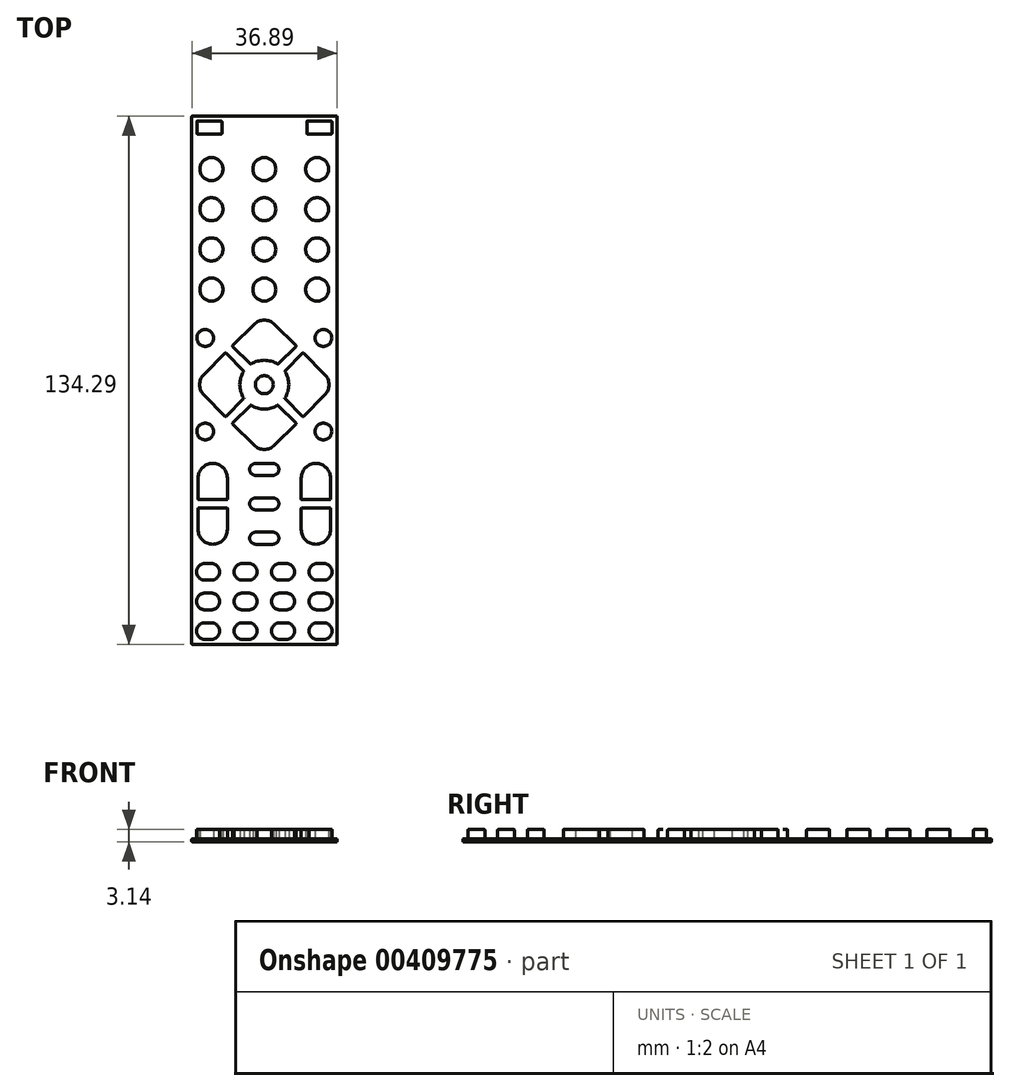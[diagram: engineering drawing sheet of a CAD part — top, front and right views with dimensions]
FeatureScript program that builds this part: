
annotation { "Feature Type Name" : "Feature", "Feature Type Description" : "" }
export const myFeature = defineFeature(function(context is Context, id is Id, definition is map)
    precondition{}
    {
        {
            var Q0;
            Q0=qCreatedBy(makeId("Top.planeOp"),FACE);
            var sketch = newSketch(context, id + "F0", { "sketchPlane" : qUnion([Q0])});
            skLineSegment(sketch, "E0", {"start": v(0, 71.3) * mm, "end": v(0, -90.63) * mm, "construction": true});
            skLineSegment(sketch, "E1.bottom", {"start": v(-17.4, 63.46) * mm, "end": v(-10.54, 63.46) * mm});
            skLineSegment(sketch, "E1.top", {"start": v(-17.4, 67.27) * mm, "end": v(-10.54, 67.27) * mm});
            skLineSegment(sketch, "E1.left", {"start": v(-17.4, 63.46) * mm, "end": v(-17.4, 67.27) * mm});
            skLineSegment(sketch, "E1.right", {"start": v(-10.54, 63.46) * mm, "end": v(-10.54, 67.27) * mm});
            skLineSegment(sketch, "E2.bottom", {"start": v(10.54, 63.46) * mm, "end": v(17.4, 63.46) * mm});
            skLineSegment(sketch, "E2.top", {"start": v(10.54, 67.27) * mm, "end": v(17.4, 67.27) * mm});
            skLineSegment(sketch, "E2.left", {"start": v(10.54, 63.46) * mm, "end": v(10.54, 67.27) * mm});
            skLineSegment(sketch, "E2.right", {"start": v(17.4, 63.46) * mm, "end": v(17.4, 67.27) * mm});
            skCircle(sketch, "E3", {"center": v(-13.44, 54.79) * mm, "radius": 3.18 * mm});
            skCircle(sketch, "E4.0.1.0", {"center": v(-13.44, 44.59) * mm, "radius": 3.18 * mm});
            skLineSegment(sketch, "E4.0.1.1", {"start": v(0, 61.1) * mm, "end": v(0, -100.83) * mm, "construction": true});
            skCircle(sketch, "E4.0.2.0", {"center": v(-13.44, 34.39) * mm, "radius": 3.18 * mm});
            skLineSegment(sketch, "E4.0.2.1", {"start": v(0, 50.9) * mm, "end": v(0, -111.03) * mm, "construction": true});
            skCircle(sketch, "E4.0.3.0", {"center": v(-13.44, 24.18) * mm, "radius": 3.18 * mm});
            skLineSegment(sketch, "E4.0.3.1", {"start": v(0, 40.7) * mm, "end": v(0, -121.23) * mm, "construction": true});
            skCircle(sketch, "E4.1.0.0", {"center": v(0, 54.79) * mm, "radius": 3.18 * mm});
            skLineSegment(sketch, "E4.1.0.1", {"start": v(13.44, 71.3) * mm, "end": v(13.44, -90.63) * mm, "construction": true});
            skCircle(sketch, "E4.1.1.0", {"center": v(0, 44.59) * mm, "radius": 3.18 * mm});
            skLineSegment(sketch, "E4.1.1.1", {"start": v(13.44, 61.1) * mm, "end": v(13.44, -100.83) * mm, "construction": true});
            skCircle(sketch, "E4.1.2.0", {"center": v(0, 34.39) * mm, "radius": 3.18 * mm});
            skLineSegment(sketch, "E4.1.2.1", {"start": v(13.44, 50.9) * mm, "end": v(13.44, -111.03) * mm, "construction": true});
            skCircle(sketch, "E4.1.3.0", {"center": v(0, 24.18) * mm, "radius": 3.18 * mm});
            skLineSegment(sketch, "E4.1.3.1", {"start": v(13.44, 40.7) * mm, "end": v(13.44, -121.23) * mm, "construction": true});
            skCircle(sketch, "E4.2.0.0", {"center": v(13.44, 54.79) * mm, "radius": 3.18 * mm});
            skLineSegment(sketch, "E4.2.0.1", {"start": v(26.87, 71.3) * mm, "end": v(26.87, -90.63) * mm, "construction": true});
            skCircle(sketch, "E4.2.1.0", {"center": v(13.44, 44.59) * mm, "radius": 3.18 * mm});
            skLineSegment(sketch, "E4.2.1.1", {"start": v(26.87, 61.1) * mm, "end": v(26.87, -100.83) * mm, "construction": true});
            skCircle(sketch, "E4.2.2.0", {"center": v(13.44, 34.39) * mm, "radius": 3.18 * mm});
            skLineSegment(sketch, "E4.2.2.1", {"start": v(26.87, 50.9) * mm, "end": v(26.87, -111.03) * mm, "construction": true});
            skCircle(sketch, "E4.2.3.0", {"center": v(13.44, 24.18) * mm, "radius": 3.18 * mm});
            skLineSegment(sketch, "E4.2.3.1", {"start": v(26.87, 40.7) * mm, "end": v(26.87, -121.23) * mm, "construction": true});
            skLineSegment(sketch, "E4.direction1", {"start": v(-13.44, 54.79) * mm, "end": v(0, 54.79) * mm, "construction": true});
            skLineSegment(sketch, "E4.direction2", {"start": v(-13.44, 54.79) * mm, "end": v(-13.44, 44.59) * mm, "construction": true});
            skCircle(sketch, "E5", {"center": v(0, 0) * mm, "radius": 2.54 * mm});
            skCircle(sketch, "E6", {"center": v(-15.02, 11.88) * mm, "radius": 2.38 * mm});
            skLineSegment(sketch, "E7", {"start": v(-22.23, 0) * mm, "end": v(22.23, 0) * mm, "construction": true});
            skCircle(sketch, "E8.MirrorC", {"center": v(15.02, 11.88) * mm, "radius": 2.38 * mm});
            skCircle(sketch, "E9.MirrorC", {"center": v(15.02, -11.88) * mm, "radius": 2.38 * mm});
            skCircle(sketch, "E10.MirrorC", {"center": v(-15.02, -11.88) * mm, "radius": 2.38 * mm});
            skArc(sketch, "E11", {"start": v(-15.54, 2.78) * mm, "mid": v(-16.7, 0) * mm, "end": v(-15.54, -2.78) * mm});
            skLineSegment(sketch, "E12", {"start": v(-15.54, 2.78) * mm, "end": v(-9.83, 8.49) * mm});
            skLineSegment(sketch, "E13", {"start": v(-9.83, 8.49) * mm, "end": v(-4.84, 3.5) * mm});
            skLineSegment(sketch, "E14", {"start": v(-15.54, -2.78) * mm, "end": v(-9.83, -8.49) * mm});
            skLineSegment(sketch, "E15", {"start": v(-9.83, -8.49) * mm, "end": v(-4.84, -3.5) * mm});
            skArc(sketch, "E16", {"start": v(-4.84, 3.5) * mm, "mid": v(-5.97, 0) * mm, "end": v(-4.84, -3.5) * mm});
            skLineSegment(sketch, "E17.MirrorCS", {"start": v(0, -61.1) * mm, "end": v(0, 100.83) * mm, "construction": true});
            skLineSegment(sketch, "E18.1.0", {"start": v(-2.78, -15.54) * mm, "end": v(-8.49, -9.83) * mm});
            skLineSegment(sketch, "E18.1.1", {"start": v(-8.49, -9.83) * mm, "end": v(-3.5, -4.84) * mm});
            skArc(sketch, "E18.1.2", {"start": v(-3.5, -4.84) * mm, "mid": v(0, -5.97) * mm, "end": v(3.5, -4.84) * mm});
            skLineSegment(sketch, "E18.1.3", {"start": v(8.49, -9.83) * mm, "end": v(3.5, -4.84) * mm});
            skLineSegment(sketch, "E18.1.4", {"start": v(2.78, -15.54) * mm, "end": v(8.49, -9.83) * mm});
            skArc(sketch, "E18.1.5", {"start": v(-2.78, -15.54) * mm, "mid": v(0, -16.7) * mm, "end": v(2.78, -15.54) * mm});
            skLineSegment(sketch, "E18.2.0", {"start": v(15.54, -2.78) * mm, "end": v(9.83, -8.49) * mm});
            skLineSegment(sketch, "E18.2.1", {"start": v(9.83, -8.49) * mm, "end": v(4.84, -3.5) * mm});
            skArc(sketch, "E18.2.2", {"start": v(4.84, -3.5) * mm, "mid": v(5.97, 0) * mm, "end": v(4.84, 3.5) * mm});
            skLineSegment(sketch, "E18.2.3", {"start": v(9.83, 8.49) * mm, "end": v(4.84, 3.5) * mm});
            skLineSegment(sketch, "E18.2.4", {"start": v(15.54, 2.78) * mm, "end": v(9.83, 8.49) * mm});
            skArc(sketch, "E18.2.5", {"start": v(15.54, -2.78) * mm, "mid": v(16.7, 0) * mm, "end": v(15.54, 2.78) * mm});
            skLineSegment(sketch, "E18.3.0", {"start": v(2.78, 15.54) * mm, "end": v(8.49, 9.83) * mm});
            skLineSegment(sketch, "E18.3.1", {"start": v(8.49, 9.83) * mm, "end": v(3.5, 4.84) * mm});
            skArc(sketch, "E18.3.2", {"start": v(3.5, 4.84) * mm, "mid": v(0, 5.97) * mm, "end": v(-3.5, 4.84) * mm});
            skLineSegment(sketch, "E18.3.3", {"start": v(-8.49, 9.83) * mm, "end": v(-3.5, 4.84) * mm});
            skLineSegment(sketch, "E18.3.4", {"start": v(-2.78, 15.54) * mm, "end": v(-8.49, 9.83) * mm});
            skArc(sketch, "E18.3.5", {"start": v(2.78, 15.54) * mm, "mid": v(0, 16.7) * mm, "end": v(-2.78, 15.54) * mm});
            skPoint(sketch, "E19.visualSharp", {"position": v(9.83, 8.49) * mm});
            skPoint(sketch, "E20.visualSharp", {"position": v(4.84, 3.5) * mm});
            skPoint(sketch, "E21.visualSharp", {"position": v(4.84, -3.5) * mm});
            skPoint(sketch, "E22.visualSharp", {"position": v(9.83, -8.49) * mm});
            skPoint(sketch, "E23.visualSharp", {"position": v(3.5, -4.84) * mm});
            skPoint(sketch, "E24.visualSharp", {"position": v(8.49, -9.83) * mm});
            skPoint(sketch, "E25.visualSharp", {"position": v(-8.49, -9.83) * mm});
            skPoint(sketch, "E26.visualSharp", {"position": v(-3.5, -4.84) * mm});
            skPoint(sketch, "E27.visualSharp", {"position": v(-9.83, -8.49) * mm});
            skPoint(sketch, "E28.visualSharp", {"position": v(-4.84, -3.5) * mm});
            skPoint(sketch, "E29.visualSharp", {"position": v(-4.84, 3.5) * mm});
            skPoint(sketch, "E30.visualSharp", {"position": v(-9.83, 8.49) * mm});
            skPoint(sketch, "E31.visualSharp", {"position": v(8.49, 9.83) * mm});
            skPoint(sketch, "E32.visualSharp", {"position": v(3.5, 4.84) * mm});
            skPoint(sketch, "E33.visualSharp", {"position": v(-3.5, 4.84) * mm});
            skPoint(sketch, "E34.visualSharp", {"position": v(-8.49, 9.83) * mm});
            skLineSegment(sketch, "E35", {"start": v(-2.18, -21.53) * mm, "end": v(2.18, -21.53) * mm, "construction": true});
            skArc(sketch, "E36.0.startCap", {"start": v(-2.18, -23.31) * mm, "mid": v(-3.97, -21.53) * mm, "end": v(-2.18, -19.74) * mm});
            skArc(sketch, "E36.0.endCap", {"start": v(2.18, -19.74) * mm, "mid": v(3.97, -21.53) * mm, "end": v(2.18, -23.31) * mm});
            skLineSegment(sketch, "E36.0.left", {"start": v(-2.18, -19.74) * mm, "end": v(2.18, -19.74) * mm});
            skLineSegment(sketch, "E36.0.right", {"start": v(-2.18, -23.31) * mm, "end": v(2.18, -23.31) * mm});
            skLineSegment(sketch, "E37.0.1.0", {"start": v(-2.18, -28.47) * mm, "end": v(2.18, -28.47) * mm});
            skArc(sketch, "E37.0.1.1", {"start": v(2.18, -28.47) * mm, "mid": v(3.97, -30.26) * mm, "end": v(2.18, -32.05) * mm});
            skLineSegment(sketch, "E37.0.1.2", {"start": v(-2.18, -32.05) * mm, "end": v(2.18, -32.05) * mm});
            skArc(sketch, "E37.0.1.3", {"start": v(-2.18, -32.05) * mm, "mid": v(-3.97, -30.26) * mm, "end": v(-2.18, -28.47) * mm});
            skLineSegment(sketch, "E37.0.2.0", {"start": v(-2.18, -37.2) * mm, "end": v(2.18, -37.2) * mm});
            skArc(sketch, "E37.0.2.1", {"start": v(2.18, -37.2) * mm, "mid": v(3.97, -39) * mm, "end": v(2.18, -40.78) * mm});
            skLineSegment(sketch, "E37.0.2.2", {"start": v(-2.18, -40.78) * mm, "end": v(2.18, -40.78) * mm});
            skArc(sketch, "E37.0.2.3", {"start": v(-2.18, -40.78) * mm, "mid": v(-3.97, -39) * mm, "end": v(-2.18, -37.2) * mm});
            skLineSegment(sketch, "E37.direction1", {"start": v(-2.18, -19.74) * mm, "end": v(23.22, -19.74) * mm, "construction": true});
            skLineSegment(sketch, "E37.direction2", {"start": v(-2.18, -19.74) * mm, "end": v(-2.18, -28.47) * mm, "construction": true});
            skLineSegment(sketch, "E38", {"start": v(-2.18, -30.26) * mm, "end": v(2.18, -30.26) * mm, "construction": true});
            skLineSegment(sketch, "E39.bottom", {"start": v(-17.07, -29.47) * mm, "end": v(-9.13, -29.47) * mm});
            skLineSegment(sketch, "E39.left", {"start": v(-17.07, -29.47) * mm, "end": v(-17.07, -23.7) * mm});
            skLineSegment(sketch, "E39.right", {"start": v(-9.13, -29.47) * mm, "end": v(-9.13, -23.7) * mm});
            skArc(sketch, "E40", {"start": v(-9.13, -23.7) * mm, "mid": v(-13.1, -19.74) * mm, "end": v(-17.07, -23.7) * mm});
            skLineSegment(sketch, "E41.MirrorCS", {"start": v(9.13, -29.47) * mm, "end": v(9.13, -23.7) * mm});
            skLineSegment(sketch, "E42.MirrorCS", {"start": v(17.07, -29.47) * mm, "end": v(9.13, -29.47) * mm});
            skLineSegment(sketch, "E43.MirrorCS", {"start": v(17.07, -29.47) * mm, "end": v(17.07, -23.7) * mm});
            skArc(sketch, "E44.MirrorCS", {"start": v(9.13, -23.7) * mm, "mid": v(13.1, -19.74) * mm, "end": v(17.07, -23.7) * mm});
            skLineSegment(sketch, "E45.MirrorCS", {"start": v(17.07, -31.05) * mm, "end": v(9.13, -31.05) * mm});
            skLineSegment(sketch, "E46.MirrorCS", {"start": v(9.13, -31.05) * mm, "end": v(9.13, -36.81) * mm});
            skArc(sketch, "E47.MirrorCS", {"start": v(9.13, -36.81) * mm, "mid": v(13.1, -40.78) * mm, "end": v(17.07, -36.81) * mm});
            skLineSegment(sketch, "E48.MirrorCS", {"start": v(17.07, -31.05) * mm, "end": v(17.07, -36.81) * mm});
            skLineSegment(sketch, "E49.MirrorCS", {"start": v(-17.07, -31.05) * mm, "end": v(-9.13, -31.05) * mm});
            skLineSegment(sketch, "E50.MirrorCS", {"start": v(-9.13, -31.05) * mm, "end": v(-9.13, -36.81) * mm});
            skLineSegment(sketch, "E51.MirrorCS", {"start": v(-17.07, -31.05) * mm, "end": v(-17.07, -36.81) * mm});
            skArc(sketch, "E52.MirrorCS", {"start": v(-9.13, -36.81) * mm, "mid": v(-13.1, -40.78) * mm, "end": v(-17.07, -36.81) * mm});
            skLineSegment(sketch, "E53", {"start": v(-15.08, -47.53) * mm, "end": v(-13.5, -47.53) * mm, "construction": true});
            skArc(sketch, "E54.0.startCap", {"start": v(-15.08, -49.9) * mm, "mid": v(-17.46, -47.53) * mm, "end": v(-15.08, -45.15) * mm});
            skArc(sketch, "E54.0.endCap", {"start": v(-13.5, -45.15) * mm, "mid": v(-11.11, -47.53) * mm, "end": v(-13.5, -49.9) * mm});
            skLineSegment(sketch, "E54.0.left", {"start": v(-15.08, -45.15) * mm, "end": v(-13.5, -45.15) * mm});
            skLineSegment(sketch, "E54.0.right", {"start": v(-15.08, -49.9) * mm, "end": v(-13.5, -49.9) * mm});
            skArc(sketch, "E55.0.1.0", {"start": v(-13.5, -52.69) * mm, "mid": v(-11.11, -55.07) * mm, "end": v(-13.5, -57.45) * mm});
            skLineSegment(sketch, "E55.0.1.1", {"start": v(-15.08, -52.69) * mm, "end": v(-13.5, -52.69) * mm});
            skArc(sketch, "E55.0.1.2", {"start": v(-15.08, -57.45) * mm, "mid": v(-17.46, -55.07) * mm, "end": v(-15.08, -52.69) * mm});
            skLineSegment(sketch, "E55.0.1.3", {"start": v(-15.08, -57.45) * mm, "end": v(-13.5, -57.45) * mm});
            skArc(sketch, "E55.0.2.0", {"start": v(-13.5, -60.23) * mm, "mid": v(-11.11, -62.6) * mm, "end": v(-13.5, -64.99) * mm});
            skLineSegment(sketch, "E55.0.2.1", {"start": v(-15.08, -60.23) * mm, "end": v(-13.5, -60.23) * mm});
            skArc(sketch, "E55.0.2.2", {"start": v(-15.08, -64.99) * mm, "mid": v(-17.46, -62.6) * mm, "end": v(-15.08, -60.23) * mm});
            skLineSegment(sketch, "E55.0.2.3", {"start": v(-15.08, -64.99) * mm, "end": v(-13.5, -64.99) * mm});
            skArc(sketch, "E55.1.0.0", {"start": v(-3.97, -45.15) * mm, "mid": v(-1.59, -47.53) * mm, "end": v(-3.97, -49.9) * mm});
            skLineSegment(sketch, "E55.1.0.1", {"start": v(-5.56, -45.15) * mm, "end": v(-3.97, -45.15) * mm});
            skArc(sketch, "E55.1.0.2", {"start": v(-5.56, -49.9) * mm, "mid": v(-7.94, -47.53) * mm, "end": v(-5.56, -45.15) * mm});
            skLineSegment(sketch, "E55.1.0.3", {"start": v(-5.56, -49.9) * mm, "end": v(-3.97, -49.9) * mm});
            skArc(sketch, "E55.1.1.0", {"start": v(-3.97, -52.69) * mm, "mid": v(-1.59, -55.07) * mm, "end": v(-3.97, -57.45) * mm});
            skLineSegment(sketch, "E55.1.1.1", {"start": v(-5.56, -52.69) * mm, "end": v(-3.97, -52.69) * mm});
            skArc(sketch, "E55.1.1.2", {"start": v(-5.56, -57.45) * mm, "mid": v(-7.94, -55.07) * mm, "end": v(-5.56, -52.69) * mm});
            skLineSegment(sketch, "E55.1.1.3", {"start": v(-5.56, -57.45) * mm, "end": v(-3.97, -57.45) * mm});
            skArc(sketch, "E55.1.2.0", {"start": v(-3.97, -60.23) * mm, "mid": v(-1.59, -62.6) * mm, "end": v(-3.97, -64.99) * mm});
            skLineSegment(sketch, "E55.1.2.1", {"start": v(-5.56, -60.23) * mm, "end": v(-3.97, -60.23) * mm});
            skArc(sketch, "E55.1.2.2", {"start": v(-5.56, -64.99) * mm, "mid": v(-7.94, -62.6) * mm, "end": v(-5.56, -60.23) * mm});
            skLineSegment(sketch, "E55.1.2.3", {"start": v(-5.56, -64.99) * mm, "end": v(-3.97, -64.99) * mm});
            skArc(sketch, "E55.2.0.0", {"start": v(5.56, -45.15) * mm, "mid": v(7.94, -47.53) * mm, "end": v(5.56, -49.9) * mm});
            skLineSegment(sketch, "E55.2.0.1", {"start": v(3.97, -45.15) * mm, "end": v(5.56, -45.15) * mm});
            skArc(sketch, "E55.2.0.2", {"start": v(3.97, -49.9) * mm, "mid": v(1.59, -47.53) * mm, "end": v(3.97, -45.15) * mm});
            skLineSegment(sketch, "E55.2.0.3", {"start": v(3.97, -49.9) * mm, "end": v(5.56, -49.9) * mm});
            skArc(sketch, "E55.2.1.0", {"start": v(5.56, -52.69) * mm, "mid": v(7.94, -55.07) * mm, "end": v(5.56, -57.45) * mm});
            skLineSegment(sketch, "E55.2.1.1", {"start": v(3.97, -52.69) * mm, "end": v(5.56, -52.69) * mm});
            skArc(sketch, "E55.2.1.2", {"start": v(3.97, -57.45) * mm, "mid": v(1.59, -55.07) * mm, "end": v(3.97, -52.69) * mm});
            skLineSegment(sketch, "E55.2.1.3", {"start": v(3.97, -57.45) * mm, "end": v(5.56, -57.45) * mm});
            skArc(sketch, "E55.2.2.0", {"start": v(5.56, -60.23) * mm, "mid": v(7.94, -62.6) * mm, "end": v(5.56, -64.99) * mm});
            skLineSegment(sketch, "E55.2.2.1", {"start": v(3.97, -60.23) * mm, "end": v(5.56, -60.23) * mm});
            skArc(sketch, "E55.2.2.2", {"start": v(3.97, -64.99) * mm, "mid": v(1.59, -62.6) * mm, "end": v(3.97, -60.23) * mm});
            skLineSegment(sketch, "E55.2.2.3", {"start": v(3.97, -64.99) * mm, "end": v(5.56, -64.99) * mm});
            skArc(sketch, "E55.3.0.0", {"start": v(15.08, -45.15) * mm, "mid": v(17.46, -47.53) * mm, "end": v(15.08, -49.9) * mm});
            skLineSegment(sketch, "E55.3.0.1", {"start": v(13.5, -45.15) * mm, "end": v(15.08, -45.15) * mm});
            skArc(sketch, "E55.3.0.2", {"start": v(13.5, -49.9) * mm, "mid": v(11.11, -47.53) * mm, "end": v(13.5, -45.15) * mm});
            skLineSegment(sketch, "E55.3.0.3", {"start": v(13.5, -49.9) * mm, "end": v(15.08, -49.9) * mm});
            skArc(sketch, "E55.3.1.0", {"start": v(15.08, -52.69) * mm, "mid": v(17.46, -55.07) * mm, "end": v(15.08, -57.45) * mm});
            skLineSegment(sketch, "E55.3.1.1", {"start": v(13.5, -52.69) * mm, "end": v(15.08, -52.69) * mm});
            skArc(sketch, "E55.3.1.2", {"start": v(13.5, -57.45) * mm, "mid": v(11.11, -55.07) * mm, "end": v(13.5, -52.69) * mm});
            skLineSegment(sketch, "E55.3.1.3", {"start": v(13.5, -57.45) * mm, "end": v(15.08, -57.45) * mm});
            skArc(sketch, "E55.3.2.0", {"start": v(15.08, -60.23) * mm, "mid": v(17.46, -62.6) * mm, "end": v(15.08, -64.99) * mm});
            skLineSegment(sketch, "E55.3.2.1", {"start": v(13.5, -60.23) * mm, "end": v(15.08, -60.23) * mm});
            skArc(sketch, "E55.3.2.2", {"start": v(13.5, -64.99) * mm, "mid": v(11.11, -62.6) * mm, "end": v(13.5, -60.23) * mm});
            skLineSegment(sketch, "E55.3.2.3", {"start": v(13.5, -64.99) * mm, "end": v(15.08, -64.99) * mm});
            skLineSegment(sketch, "E55.direction1", {"start": v(-13.5, -49.9) * mm, "end": v(-3.97, -49.9) * mm, "construction": true});
            skLineSegment(sketch, "E55.direction2", {"start": v(-13.5, -49.9) * mm, "end": v(-13.5, -57.45) * mm, "construction": true});
            skLineSegment(sketch, "E56.bottom", {"start": v(-18.73, 68.54) * mm, "end": v(18.73, 68.54) * mm});
            skLineSegment(sketch, "E56.top", {"start": v(-18.73, -66.26) * mm, "end": v(18.73, -66.26) * mm});
            skLineSegment(sketch, "E56.left", {"start": v(-18.73, 68.54) * mm, "end": v(-18.73, -66.26) * mm});
            skLineSegment(sketch, "E56.right", {"start": v(18.73, 68.54) * mm, "end": v(18.73, -66.26) * mm});
            skSolve(sketch);
        }
        {
            var Q0;
            Q0=qCreatedBy(makeId("Top.planeOp"),FACE);
            var sketch = newSketch(context, id + "F1", { "sketchPlane" : qUnion([Q0])});
            skLineSegment(sketch, "E57.0", {"start": v(-10.8, 67.01) * mm, "end": v(-17.14, 67.01) * mm});
            skLineSegment(sketch, "E57.1", {"start": v(-10.8, 63.7) * mm, "end": v(-10.8, 67.01) * mm});
            skLineSegment(sketch, "E57.2", {"start": v(-17.14, 63.7) * mm, "end": v(-10.8, 63.7) * mm});
            skLineSegment(sketch, "E57.3", {"start": v(-17.14, 67.01) * mm, "end": v(-17.14, 63.7) * mm});
            skCircle(sketch, "E58.0", {"center": v(-13.44, 54.79) * mm, "radius": 2.92 * mm});
            skCircle(sketch, "E59.0", {"center": v(0, 54.79) * mm, "radius": 2.92 * mm});
            skCircle(sketch, "E60.0", {"center": v(13.44, 54.79) * mm, "radius": 2.92 * mm});
            skCircle(sketch, "E61.0", {"center": v(-13.44, 44.59) * mm, "radius": 2.92 * mm});
            skCircle(sketch, "E62.0", {"center": v(0, 44.59) * mm, "radius": 2.92 * mm});
            skCircle(sketch, "E63.0", {"center": v(13.44, 44.59) * mm, "radius": 2.92 * mm});
            skCircle(sketch, "E64.0", {"center": v(-13.44, 34.39) * mm, "radius": 2.92 * mm});
            skCircle(sketch, "E65.0", {"center": v(0, 34.39) * mm, "radius": 2.92 * mm});
            skCircle(sketch, "E66.0", {"center": v(13.44, 34.39) * mm, "radius": 2.92 * mm});
            skCircle(sketch, "E67.0", {"center": v(-13.44, 24.18) * mm, "radius": 2.92 * mm});
            skCircle(sketch, "E68.0", {"center": v(0, 24.18) * mm, "radius": 2.92 * mm});
            skCircle(sketch, "E69.0", {"center": v(13.44, 24.18) * mm, "radius": 2.92 * mm});
            skCircle(sketch, "E70.0", {"center": v(-15.02, 11.88) * mm, "radius": 2.13 * mm});
            skCircle(sketch, "E71.0", {"center": v(15.02, 11.88) * mm, "radius": 2.13 * mm});
            skLineSegment(sketch, "E72.0", {"start": v(3.46, 5.17) * mm, "end": v(8.13, 9.83) * mm});
            skArc(sketch, "E72.1", {"start": v(2.6, 15.36) * mm, "mid": v(0, 16.44) * mm, "end": v(-2.6, 15.36) * mm});
            skLineSegment(sketch, "E72.2", {"start": v(-2.6, 15.36) * mm, "end": v(-8.13, 9.83) * mm});
            skLineSegment(sketch, "E72.3", {"start": v(8.13, 9.83) * mm, "end": v(2.6, 15.36) * mm});
            skLineSegment(sketch, "E72.4", {"start": v(-8.13, 9.83) * mm, "end": v(-3.46, 5.17) * mm});
            skArc(sketch, "E72.5", {"start": v(-3.46, 5.17) * mm, "mid": v(0, 6.22) * mm, "end": v(3.46, 5.17) * mm});
            skLineSegment(sketch, "E73.0", {"start": v(5.17, -3.46) * mm, "end": v(9.83, -8.13) * mm});
            skArc(sketch, "E73.1", {"start": v(15.36, -2.6) * mm, "mid": v(16.44, 0) * mm, "end": v(15.36, 2.6) * mm});
            skLineSegment(sketch, "E73.2", {"start": v(15.36, 2.6) * mm, "end": v(9.83, 8.13) * mm});
            skLineSegment(sketch, "E73.3", {"start": v(9.83, -8.13) * mm, "end": v(15.36, -2.6) * mm});
            skLineSegment(sketch, "E73.4", {"start": v(9.83, 8.13) * mm, "end": v(5.17, 3.46) * mm});
            skArc(sketch, "E73.5", {"start": v(5.17, 3.46) * mm, "mid": v(6.22, 0) * mm, "end": v(5.17, -3.46) * mm});
            skLineSegment(sketch, "E74.0", {"start": v(-9.83, -8.13) * mm, "end": v(-5.17, -3.46) * mm});
            skLineSegment(sketch, "E74.1", {"start": v(-5.17, 3.46) * mm, "end": v(-9.83, 8.13) * mm});
            skLineSegment(sketch, "E74.2", {"start": v(-9.83, 8.13) * mm, "end": v(-15.36, 2.6) * mm});
            skArc(sketch, "E74.3", {"start": v(-5.17, -3.46) * mm, "mid": v(-6.22, 0) * mm, "end": v(-5.17, 3.46) * mm});
            skArc(sketch, "E74.4", {"start": v(-15.36, 2.6) * mm, "mid": v(-16.44, 0) * mm, "end": v(-15.36, -2.6) * mm});
            skLineSegment(sketch, "E74.5", {"start": v(-15.36, -2.6) * mm, "end": v(-9.83, -8.13) * mm});
            skCircle(sketch, "E75.0", {"center": v(0, 0) * mm, "radius": 2.29 * mm});
            skCircle(sketch, "E76.0", {"center": v(15.02, -11.88) * mm, "radius": 2.13 * mm});
            skLineSegment(sketch, "E77.0", {"start": v(-3.46, -5.17) * mm, "end": v(-8.13, -9.83) * mm});
            skArc(sketch, "E77.1", {"start": v(-2.6, -15.36) * mm, "mid": v(0, -16.44) * mm, "end": v(2.6, -15.36) * mm});
            skLineSegment(sketch, "E77.2", {"start": v(2.6, -15.36) * mm, "end": v(8.13, -9.83) * mm});
            skLineSegment(sketch, "E77.3", {"start": v(-8.13, -9.83) * mm, "end": v(-2.6, -15.36) * mm});
            skLineSegment(sketch, "E77.4", {"start": v(8.13, -9.83) * mm, "end": v(3.46, -5.17) * mm});
            skArc(sketch, "E77.5", {"start": v(3.46, -5.17) * mm, "mid": v(0, -6.22) * mm, "end": v(-3.46, -5.17) * mm});
            skCircle(sketch, "E78.0", {"center": v(-15.02, -11.88) * mm, "radius": 2.13 * mm});
            skLineSegment(sketch, "E79.0", {"start": v(-9.38, -29.21) * mm, "end": v(-9.38, -23.7) * mm});
            skLineSegment(sketch, "E79.1", {"start": v(-16.81, -29.21) * mm, "end": v(-9.38, -29.21) * mm});
            skLineSegment(sketch, "E79.2", {"start": v(-16.81, -23.7) * mm, "end": v(-16.81, -29.21) * mm});
            skArc(sketch, "E79.3", {"start": v(-9.38, -23.7) * mm, "mid": v(-13.1, -20) * mm, "end": v(-16.81, -23.7) * mm});
            skArc(sketch, "E80.0", {"start": v(2.18, -23.06) * mm, "mid": v(3.71, -21.53) * mm, "end": v(2.18, -20) * mm});
            skLineSegment(sketch, "E80.1", {"start": v(-2.18, -23.06) * mm, "end": v(2.18, -23.06) * mm});
            skArc(sketch, "E80.2", {"start": v(-2.18, -20) * mm, "mid": v(-3.71, -21.53) * mm, "end": v(-2.18, -23.06) * mm});
            skLineSegment(sketch, "E80.3", {"start": v(2.18, -20) * mm, "end": v(-2.18, -20) * mm});
            skArc(sketch, "E81.0", {"start": v(16.81, -23.7) * mm, "mid": v(13.1, -20) * mm, "end": v(9.38, -23.7) * mm});
            skLineSegment(sketch, "E81.1", {"start": v(16.81, -29.21) * mm, "end": v(16.81, -23.7) * mm});
            skLineSegment(sketch, "E81.2", {"start": v(9.38, -29.21) * mm, "end": v(16.81, -29.21) * mm});
            skLineSegment(sketch, "E81.3", {"start": v(9.38, -23.7) * mm, "end": v(9.38, -29.21) * mm});
            skArc(sketch, "E82.0", {"start": v(-16.81, -36.81) * mm, "mid": v(-13.1, -40.53) * mm, "end": v(-9.38, -36.81) * mm});
            skLineSegment(sketch, "E82.1", {"start": v(-16.81, -31.3) * mm, "end": v(-16.81, -36.81) * mm});
            skLineSegment(sketch, "E82.2", {"start": v(-9.38, -31.3) * mm, "end": v(-16.81, -31.3) * mm});
            skLineSegment(sketch, "E82.3", {"start": v(-9.38, -36.81) * mm, "end": v(-9.38, -31.3) * mm});
            skArc(sketch, "E83.0", {"start": v(-2.18, -28.73) * mm, "mid": v(-3.71, -30.26) * mm, "end": v(-2.18, -31.8) * mm});
            skLineSegment(sketch, "E83.1", {"start": v(2.18, -28.73) * mm, "end": v(-2.18, -28.73) * mm});
            skArc(sketch, "E83.2", {"start": v(2.18, -31.8) * mm, "mid": v(3.71, -30.26) * mm, "end": v(2.18, -28.73) * mm});
            skLineSegment(sketch, "E83.3", {"start": v(-2.18, -31.8) * mm, "end": v(2.18, -31.8) * mm});
            skLineSegment(sketch, "E84.0", {"start": v(16.81, -36.81) * mm, "end": v(16.81, -31.3) * mm});
            skArc(sketch, "E84.1", {"start": v(9.38, -36.81) * mm, "mid": v(13.1, -40.53) * mm, "end": v(16.81, -36.81) * mm});
            skLineSegment(sketch, "E84.2", {"start": v(9.38, -31.3) * mm, "end": v(9.38, -36.81) * mm});
            skLineSegment(sketch, "E84.3", {"start": v(16.81, -31.3) * mm, "end": v(9.38, -31.3) * mm});
            skArc(sketch, "E85.0", {"start": v(-2.18, -37.46) * mm, "mid": v(-3.71, -39) * mm, "end": v(-2.18, -40.53) * mm});
            skLineSegment(sketch, "E85.1", {"start": v(2.18, -37.46) * mm, "end": v(-2.18, -37.46) * mm});
            skArc(sketch, "E85.2", {"start": v(2.18, -40.53) * mm, "mid": v(3.71, -39) * mm, "end": v(2.18, -37.46) * mm});
            skLineSegment(sketch, "E85.3", {"start": v(-2.18, -40.53) * mm, "end": v(2.18, -40.53) * mm});
            skArc(sketch, "E86.0", {"start": v(-15.08, -52.94) * mm, "mid": v(-17.2, -55.07) * mm, "end": v(-15.08, -57.2) * mm});
            skLineSegment(sketch, "E86.1", {"start": v(-13.5, -52.94) * mm, "end": v(-15.08, -52.94) * mm});
            skArc(sketch, "E86.2", {"start": v(-13.5, -57.2) * mm, "mid": v(-11.37, -55.07) * mm, "end": v(-13.5, -52.94) * mm});
            skLineSegment(sketch, "E86.3", {"start": v(-15.08, -57.2) * mm, "end": v(-13.5, -57.2) * mm});
            skArc(sketch, "E87.0", {"start": v(-5.56, -52.94) * mm, "mid": v(-7.68, -55.07) * mm, "end": v(-5.56, -57.2) * mm});
            skLineSegment(sketch, "E87.1", {"start": v(-3.97, -52.94) * mm, "end": v(-5.56, -52.94) * mm});
            skArc(sketch, "E87.2", {"start": v(-3.97, -57.2) * mm, "mid": v(-1.84, -55.07) * mm, "end": v(-3.97, -52.94) * mm});
            skLineSegment(sketch, "E87.3", {"start": v(-5.56, -57.2) * mm, "end": v(-3.97, -57.2) * mm});
            skArc(sketch, "E88.0", {"start": v(3.97, -52.94) * mm, "mid": v(1.84, -55.07) * mm, "end": v(3.97, -57.2) * mm});
            skLineSegment(sketch, "E88.1", {"start": v(5.56, -52.94) * mm, "end": v(3.97, -52.94) * mm});
            skArc(sketch, "E88.2", {"start": v(5.56, -57.2) * mm, "mid": v(7.68, -55.07) * mm, "end": v(5.56, -52.94) * mm});
            skLineSegment(sketch, "E88.3", {"start": v(3.97, -57.2) * mm, "end": v(5.56, -57.2) * mm});
            skArc(sketch, "E89.0", {"start": v(13.5, -52.94) * mm, "mid": v(11.37, -55.07) * mm, "end": v(13.5, -57.2) * mm});
            skLineSegment(sketch, "E89.1", {"start": v(15.08, -52.94) * mm, "end": v(13.5, -52.94) * mm});
            skArc(sketch, "E89.2", {"start": v(15.08, -57.2) * mm, "mid": v(17.2, -55.07) * mm, "end": v(15.08, -52.94) * mm});
            skLineSegment(sketch, "E89.3", {"start": v(13.5, -57.2) * mm, "end": v(15.08, -57.2) * mm});
            skArc(sketch, "E90.0", {"start": v(-15.08, -60.48) * mm, "mid": v(-17.2, -62.6) * mm, "end": v(-15.08, -64.74) * mm});
            skLineSegment(sketch, "E90.1", {"start": v(-13.5, -60.48) * mm, "end": v(-15.08, -60.48) * mm});
            skArc(sketch, "E90.2", {"start": v(-13.5, -64.74) * mm, "mid": v(-11.37, -62.6) * mm, "end": v(-13.5, -60.48) * mm});
            skLineSegment(sketch, "E90.3", {"start": v(-15.08, -64.74) * mm, "end": v(-13.5, -64.74) * mm});
            skArc(sketch, "E91.0", {"start": v(-5.56, -60.48) * mm, "mid": v(-7.68, -62.6) * mm, "end": v(-5.56, -64.74) * mm});
            skLineSegment(sketch, "E91.1", {"start": v(-3.97, -60.48) * mm, "end": v(-5.56, -60.48) * mm});
            skArc(sketch, "E91.2", {"start": v(-3.97, -64.74) * mm, "mid": v(-1.84, -62.6) * mm, "end": v(-3.97, -60.48) * mm});
            skLineSegment(sketch, "E91.3", {"start": v(-5.56, -64.74) * mm, "end": v(-3.97, -64.74) * mm});
            skArc(sketch, "E92.0", {"start": v(3.97, -60.48) * mm, "mid": v(1.84, -62.6) * mm, "end": v(3.97, -64.74) * mm});
            skLineSegment(sketch, "E92.1", {"start": v(5.56, -60.48) * mm, "end": v(3.97, -60.48) * mm});
            skArc(sketch, "E92.2", {"start": v(5.56, -64.74) * mm, "mid": v(7.68, -62.6) * mm, "end": v(5.56, -60.48) * mm});
            skLineSegment(sketch, "E92.3", {"start": v(3.97, -64.74) * mm, "end": v(5.56, -64.74) * mm});
            skArc(sketch, "E93.0", {"start": v(13.5, -60.48) * mm, "mid": v(11.37, -62.6) * mm, "end": v(13.5, -64.74) * mm});
            skLineSegment(sketch, "E93.1", {"start": v(15.08, -60.48) * mm, "end": v(13.5, -60.48) * mm});
            skArc(sketch, "E93.2", {"start": v(15.08, -64.74) * mm, "mid": v(17.2, -62.6) * mm, "end": v(15.08, -60.48) * mm});
            skLineSegment(sketch, "E93.3", {"start": v(13.5, -64.74) * mm, "end": v(15.08, -64.74) * mm});
            skSolve(sketch);
        }
        {
            var Q0;
            Q0=qCreatedBy(makeId("Top.planeOp"),FACE);
            var sketch = newSketch(context, id + "F2", { "sketchPlane" : qUnion([Q0])});
            skLineSegment(sketch, "E94.bottom", {"start": v(18.48, -66) * mm, "end": v(-18.41, -66) * mm});
            skLineSegment(sketch, "E94.top", {"start": v(18.48, 68.28) * mm, "end": v(-18.41, 68.28) * mm});
            skLineSegment(sketch, "E94.left", {"start": v(18.48, -66) * mm, "end": v(18.48, 68.28) * mm});
            skLineSegment(sketch, "E94.right", {"start": v(-18.41, -66) * mm, "end": v(-18.41, 68.28) * mm});
            skSolve(sketch);
        }
        {
            var Q0;
            Q0 = qSketchRegion(id + "F2", true);
            extrude(context, id + "F3", {"entities" : qUnion([Q0]), "oppositeDirection" : true, "depth" : 0.8 * mm});
        }
        {
            var Q0;
            Q0 = qSketchRegion(id + "F1", true);
            extrude(context, id + "F4", {"entities" : qUnion([Q0]), "operationType" : NewBodyOperationType.ADD, "depth" : 2.35 * mm});
        }
        {
            var Q0;
            Q0=makeQuery(id+"F0.imprint","IMPRINT",FACE,{"disambiguationData":[TD([[makeQuery(id+"F0.imprint","IMPRINT",EDGE,{"derivedFrom":sQuery(id+"F0.wireOp",EDGE,"E1.bottom")}),-1.0]])]});
            var sketch = newSketch(context, id + "F5", { "sketchPlane" : qUnion([Q0])});
            skLineSegment(sketch, "E95.0", {"start": v(17.14, 67.01) * mm, "end": v(10.8, 67.01) * mm});
            skLineSegment(sketch, "E95.1", {"start": v(17.14, 63.7) * mm, "end": v(17.14, 67.01) * mm});
            skLineSegment(sketch, "E95.2", {"start": v(10.8, 63.7) * mm, "end": v(17.14, 63.7) * mm});
            skLineSegment(sketch, "E95.3", {"start": v(10.8, 67.01) * mm, "end": v(10.8, 63.7) * mm});
            skArc(sketch, "E96.0", {"start": v(-13.5, -49.65) * mm, "mid": v(-11.37, -47.53) * mm, "end": v(-13.5, -45.4) * mm});
            skLineSegment(sketch, "E96.1", {"start": v(-15.08, -49.65) * mm, "end": v(-13.5, -49.65) * mm});
            skArc(sketch, "E96.2", {"start": v(-15.08, -45.4) * mm, "mid": v(-17.2, -47.53) * mm, "end": v(-15.08, -49.65) * mm});
            skLineSegment(sketch, "E96.3", {"start": v(-13.5, -45.4) * mm, "end": v(-15.08, -45.4) * mm});
            skArc(sketch, "E97.0", {"start": v(-5.56, -45.4) * mm, "mid": v(-7.68, -47.53) * mm, "end": v(-5.56, -49.65) * mm});
            skLineSegment(sketch, "E97.1", {"start": v(-3.97, -45.4) * mm, "end": v(-5.56, -45.4) * mm});
            skArc(sketch, "E97.2", {"start": v(-3.97, -49.65) * mm, "mid": v(-1.84, -47.53) * mm, "end": v(-3.97, -45.4) * mm});
            skLineSegment(sketch, "E97.3", {"start": v(-5.56, -49.65) * mm, "end": v(-3.97, -49.65) * mm});
            skArc(sketch, "E98.0", {"start": v(3.97, -45.4) * mm, "mid": v(1.84, -47.53) * mm, "end": v(3.97, -49.65) * mm});
            skLineSegment(sketch, "E98.1", {"start": v(5.56, -45.4) * mm, "end": v(3.97, -45.4) * mm});
            skArc(sketch, "E98.2", {"start": v(5.56, -49.65) * mm, "mid": v(7.68, -47.53) * mm, "end": v(5.56, -45.4) * mm});
            skLineSegment(sketch, "E98.3", {"start": v(3.97, -49.65) * mm, "end": v(5.56, -49.65) * mm});
            skArc(sketch, "E99.0", {"start": v(13.5, -45.4) * mm, "mid": v(11.37, -47.53) * mm, "end": v(13.5, -49.65) * mm});
            skLineSegment(sketch, "E99.1", {"start": v(15.08, -45.4) * mm, "end": v(13.5, -45.4) * mm});
            skArc(sketch, "E99.2", {"start": v(15.08, -49.65) * mm, "mid": v(17.2, -47.53) * mm, "end": v(15.08, -45.4) * mm});
            skLineSegment(sketch, "E99.3", {"start": v(13.5, -49.65) * mm, "end": v(15.08, -49.65) * mm});
            skSolve(sketch);
        }
        {
            var Q0;
            Q0 = qSketchRegion(id + "F5", true);
            var Q1;
            Q1=makeQuery(id+"F4.opExtrude","CAP_FACE",FACE,{"disambiguationData":[OSD([sQuery(id+"F1.wireOp",EDGE,"E82.0"),sQuery(id+"F1.wireOp",EDGE,"E82.1"),sQuery(id+"F1.wireOp",EDGE,"E82.2"),sQuery(id+"F1.wireOp",EDGE,"E82.3")])],"isStart":false});
            extrude(context, id + "F6", {"entities" : qUnion([Q0]), "endBound" : BoundingType.UP_TO_SURFACE, "endBoundEntityFace" : qUnion([Q1]), "depth" : 25.4 * mm});
        }
        {
            var Q0;
            Q0=makeQuery(id+"F3.opExtrude","CAP_EDGE",EDGE,{"disambiguationData":[OSD([sQuery(id+"F2.wireOp",EDGE,"E94.left")])],"isStart":true});
            var Q1;
            Q1=makeQuery(id+"F3.opExtrude","CAP_EDGE",EDGE,{"disambiguationData":[OSD([sQuery(id+"F2.wireOp",EDGE,"E94.right")])],"isStart":true});
            var Q2;
            Q2=makeQuery(id+"F3.opExtrude","CAP_EDGE",EDGE,{"disambiguationData":[OSD([sQuery(id+"F2.wireOp",EDGE,"E94.bottom")])],"isStart":true});
            var Q3;
            Q3=makeQuery(id+"F4.opExtrude","CAP_EDGE",EDGE,{"disambiguationData":[OSD([sQuery(id+"F1.wireOp",EDGE,"E84.0")])],"isStart":true});
            var Q4;
            Q4=makeQuery(id+"F4.opExtrude","CAP_EDGE",EDGE,{"disambiguationData":[OSD([sQuery(id+"F1.wireOp",EDGE,"E81.3")])],"isStart":false});
            var Q5;
            Q5=makeQuery(id+"F4.opExtrude","CAP_EDGE",EDGE,{"disambiguationData":[OSD([sQuery(id+"F1.wireOp",EDGE,"E81.1")])],"isStart":false});
            var Q6;
            Q6=makeQuery(id+"F4.opExtrude","CAP_EDGE",EDGE,{"disambiguationData":[OSD([sQuery(id+"F1.wireOp",EDGE,"E84.2")])],"isStart":false});
            var Q7;
            Q7=makeQuery(id+"F4.opExtrude","CAP_EDGE",EDGE,{"disambiguationData":[OSD([sQuery(id+"F1.wireOp",EDGE,"E81.2")])],"isStart":false});
            var Q8;
            Q8=makeQuery(id+"F4.opExtrude","SWEPT_EDGE",EDGE,{"disambiguationData":[OSD([sQuery(id+"F1.wireOp",EDGE,"E73.0"),sQuery(id+"F1.wireOp",EDGE,"E73.3")])]});
            var Q9;
            Q9=makeQuery(id+"F4.opExtrude","CAP_EDGE",EDGE,{"disambiguationData":[OSD([sQuery(id+"F1.wireOp",EDGE,"E84.0")])],"isStart":false});
            var Q10;
            Q10=makeQuery(id+"F6.opExtrude","CAP_EDGE",EDGE,{"disambiguationData":[OSD([sQuery(id+"F5.wireOp",EDGE,"E99.0")])],"isStart":false});
            var Q11;
            Q11=makeQuery(id+"F6.opExtrude","SWEPT_EDGE",EDGE,{"disambiguationData":[OSD([sQuery(id+"F5.wireOp",EDGE,"E99.0"),sQuery(id+"F5.wireOp",EDGE,"E99.1")])]});
            var Q12;
            Q12=makeQuery(id+"F6.opExtrude","SWEPT_EDGE",EDGE,{"disambiguationData":[OSD([sQuery(id+"F5.wireOp",EDGE,"E99.1"),sQuery(id+"F5.wireOp",EDGE,"E99.2")])]});
            var Q13;
            Q13=makeQuery(id+"F6.opExtrude","SWEPT_EDGE",EDGE,{"disambiguationData":[OSD([sQuery(id+"F5.wireOp",EDGE,"E99.2"),sQuery(id+"F5.wireOp",EDGE,"E99.3")])]});
            var Q14;
            Q14=makeQuery(id+"F6.opExtrude","SWEPT_EDGE",EDGE,{"disambiguationData":[OSD([sQuery(id+"F5.wireOp",EDGE,"E99.0"),sQuery(id+"F5.wireOp",EDGE,"E99.3")])]});
            var Q15;
            Q15=makeQuery(id+"F6.opExtrude","CAP_EDGE",EDGE,{"disambiguationData":[OSD([sQuery(id+"F5.wireOp",EDGE,"E99.2")])],"isStart":false});
            var Q16;
            Q16=makeQuery(id+"F6.opExtrude","CAP_EDGE",EDGE,{"disambiguationData":[OSD([sQuery(id+"F5.wireOp",EDGE,"E98.0")])],"isStart":false});
            var Q17;
            Q17=makeQuery(id+"F6.opExtrude","SWEPT_EDGE",EDGE,{"disambiguationData":[OSD([sQuery(id+"F5.wireOp",EDGE,"E98.0"),sQuery(id+"F5.wireOp",EDGE,"E98.1")])]});
            var Q18;
            Q18=makeQuery(id+"F6.opExtrude","SWEPT_EDGE",EDGE,{"disambiguationData":[OSD([sQuery(id+"F5.wireOp",EDGE,"E98.1"),sQuery(id+"F5.wireOp",EDGE,"E98.2")])]});
            var Q19;
            Q19=makeQuery(id+"F6.opExtrude","SWEPT_EDGE",EDGE,{"disambiguationData":[OSD([sQuery(id+"F5.wireOp",EDGE,"E98.2"),sQuery(id+"F5.wireOp",EDGE,"E98.3")])]});
            var Q20;
            Q20=makeQuery(id+"F6.opExtrude","SWEPT_EDGE",EDGE,{"disambiguationData":[OSD([sQuery(id+"F5.wireOp",EDGE,"E98.0"),sQuery(id+"F5.wireOp",EDGE,"E98.3")])]});
            var Q21;
            Q21=makeQuery(id+"F6.opExtrude","CAP_EDGE",EDGE,{"disambiguationData":[OSD([sQuery(id+"F5.wireOp",EDGE,"E98.2")])],"isStart":false});
            var Q22;
            Q22=makeQuery(id+"F6.opExtrude","SWEPT_EDGE",EDGE,{"disambiguationData":[OSD([sQuery(id+"F5.wireOp",EDGE,"E95.1"),sQuery(id+"F5.wireOp",EDGE,"E95.2")])]});
            var Q23;
            Q23=makeQuery(id+"F6.opExtrude","SWEPT_EDGE",EDGE,{"disambiguationData":[OSD([sQuery(id+"F5.wireOp",EDGE,"E95.0"),sQuery(id+"F5.wireOp",EDGE,"E95.1")])]});
            var Q24;
            Q24=makeQuery(id+"F4.opExtrude","CAP_EDGE",EDGE,{"disambiguationData":[OSD([sQuery(id+"F1.wireOp",EDGE,"E93.0")])],"isStart":true});
            var Q25;
            Q25=makeQuery(id+"F4.opExtrude","CAP_EDGE",EDGE,{"disambiguationData":[OSD([sQuery(id+"F1.wireOp",EDGE,"E93.3")])],"isStart":true});
            var Q26;
            Q26=makeQuery(id+"F4.opExtrude","CAP_EDGE",EDGE,{"disambiguationData":[OSD([sQuery(id+"F1.wireOp",EDGE,"E93.2")])],"isStart":true});
            var Q27;
            Q27=makeQuery(id+"F4.opExtrude","CAP_EDGE",EDGE,{"disambiguationData":[OSD([sQuery(id+"F1.wireOp",EDGE,"E93.0")])],"isStart":false});
            var Q28;
            Q28=makeQuery(id+"F4.opExtrude","CAP_EDGE",EDGE,{"disambiguationData":[OSD([sQuery(id+"F1.wireOp",EDGE,"E93.3")])],"isStart":false});
            var Q29;
            Q29=makeQuery(id+"F4.opExtrude","CAP_EDGE",EDGE,{"disambiguationData":[OSD([sQuery(id+"F1.wireOp",EDGE,"E93.2")])],"isStart":false});
            var Q30;
            Q30=makeQuery(id+"F4.opExtrude","SWEPT_EDGE",EDGE,{"disambiguationData":[OSD([sQuery(id+"F1.wireOp",EDGE,"E93.0"),sQuery(id+"F1.wireOp",EDGE,"E93.1")])]});
            var Q31;
            Q31=makeQuery(id+"F4.opExtrude","CAP_EDGE",EDGE,{"disambiguationData":[OSD([sQuery(id+"F1.wireOp",EDGE,"E92.0")])],"isStart":true});
            var Q32;
            Q32=makeQuery(id+"F4.opExtrude","CAP_EDGE",EDGE,{"disambiguationData":[OSD([sQuery(id+"F1.wireOp",EDGE,"E92.3")])],"isStart":true});
            var Q33;
            Q33=makeQuery(id+"F4.opExtrude","CAP_EDGE",EDGE,{"disambiguationData":[OSD([sQuery(id+"F1.wireOp",EDGE,"E92.2")])],"isStart":true});
            var Q34;
            Q34=makeQuery(id+"F4.opExtrude","CAP_EDGE",EDGE,{"disambiguationData":[OSD([sQuery(id+"F1.wireOp",EDGE,"E92.0")])],"isStart":false});
            var Q35;
            Q35=makeQuery(id+"F4.opExtrude","CAP_EDGE",EDGE,{"disambiguationData":[OSD([sQuery(id+"F1.wireOp",EDGE,"E92.3")])],"isStart":false});
            var Q36;
            Q36=makeQuery(id+"F4.opExtrude","CAP_EDGE",EDGE,{"disambiguationData":[OSD([sQuery(id+"F1.wireOp",EDGE,"E92.2")])],"isStart":false});
            var Q37;
            Q37=makeQuery(id+"F4.opExtrude","CAP_EDGE",EDGE,{"disambiguationData":[OSD([sQuery(id+"F1.wireOp",EDGE,"E90.0")])],"isStart":true});
            var Q38;
            Q38=makeQuery(id+"F4.opExtrude","CAP_EDGE",EDGE,{"disambiguationData":[OSD([sQuery(id+"F1.wireOp",EDGE,"E90.3")])],"isStart":true});
            var Q39;
            Q39=makeQuery(id+"F4.opExtrude","CAP_EDGE",EDGE,{"disambiguationData":[OSD([sQuery(id+"F1.wireOp",EDGE,"E90.2")])],"isStart":true});
            var Q40;
            Q40=makeQuery(id+"F4.opExtrude","CAP_EDGE",EDGE,{"disambiguationData":[OSD([sQuery(id+"F1.wireOp",EDGE,"E90.0")])],"isStart":false});
            var Q41;
            Q41=makeQuery(id+"F4.opExtrude","CAP_EDGE",EDGE,{"disambiguationData":[OSD([sQuery(id+"F1.wireOp",EDGE,"E90.3")])],"isStart":false});
            var Q42;
            Q42=makeQuery(id+"F4.opExtrude","CAP_EDGE",EDGE,{"disambiguationData":[OSD([sQuery(id+"F1.wireOp",EDGE,"E90.2")])],"isStart":false});
            var Q43;
            Q43=makeQuery(id+"F4.opExtrude","SWEPT_EDGE",EDGE,{"disambiguationData":[OSD([sQuery(id+"F1.wireOp",EDGE,"E90.0"),sQuery(id+"F1.wireOp",EDGE,"E90.1")])]});
            var Q44;
            Q44=makeQuery(id+"F4.opExtrude","CAP_EDGE",EDGE,{"disambiguationData":[OSD([sQuery(id+"F1.wireOp",EDGE,"E57.2")])],"isStart":true});
            var Q45;
            Q45=makeQuery(id+"F3.opExtrude","CAP_EDGE",EDGE,{"disambiguationData":[OSD([sQuery(id+"F2.wireOp",EDGE,"E94.top")])],"isStart":true});
            var Q46;
            Q46=makeQuery(id+"F3.opExtrude","CAP_EDGE",EDGE,{"disambiguationData":[OSD([sQuery(id+"F2.wireOp",EDGE,"E94.left")])],"isStart":false});
            var Q47;
            Q47=makeQuery(id+"F3.opExtrude","CAP_EDGE",EDGE,{"disambiguationData":[OSD([sQuery(id+"F2.wireOp",EDGE,"E94.top")])],"isStart":false});
            var Q48;
            Q48=makeQuery(id+"F3.opExtrude","CAP_EDGE",EDGE,{"disambiguationData":[OSD([sQuery(id+"F2.wireOp",EDGE,"E94.right")])],"isStart":false});
            var Q49;
            Q49=makeQuery(id+"F3.opExtrude","CAP_EDGE",EDGE,{"disambiguationData":[OSD([sQuery(id+"F2.wireOp",EDGE,"E94.bottom")])],"isStart":false});
            var Q50;
            Q50=makeQuery(id+"F4.opExtrude","SWEPT_EDGE",EDGE,{"disambiguationData":[OSD([sQuery(id+"F1.wireOp",EDGE,"E90.0"),sQuery(id+"F1.wireOp",EDGE,"E90.3")])]});
            var Q51;
            Q51=makeQuery(id+"F4.opExtrude","SWEPT_EDGE",EDGE,{"disambiguationData":[OSD([sQuery(id+"F1.wireOp",EDGE,"E92.1"),sQuery(id+"F1.wireOp",EDGE,"E92.2")])]});
            var Q52;
            Q52=makeQuery(id+"F4.opExtrude","SWEPT_EDGE",EDGE,{"disambiguationData":[OSD([sQuery(id+"F1.wireOp",EDGE,"E93.0"),sQuery(id+"F1.wireOp",EDGE,"E93.3")])]});
            var Q53;
            Q53=makeQuery(id+"F4.opExtrude","CAP_EDGE",EDGE,{"disambiguationData":[OSD([sQuery(id+"F1.wireOp",EDGE,"E88.2")])],"isStart":true});
            var Q54;
            Q54=makeQuery(id+"F3.opExtrude","SWEPT_EDGE",EDGE,{"disambiguationData":[OSD([sQuery(id+"F2.wireOp",EDGE,"E94.bottom"),sQuery(id+"F2.wireOp",EDGE,"E94.left")])]});
            var Q55;
            Q55=makeQuery(id+"F3.opExtrude","SWEPT_EDGE",EDGE,{"disambiguationData":[OSD([sQuery(id+"F2.wireOp",EDGE,"E94.bottom"),sQuery(id+"F2.wireOp",EDGE,"E94.right")])]});
            var Q56;
            Q56=makeQuery(id+"F4.opExtrude","CAP_EDGE",EDGE,{"disambiguationData":[OSD([sQuery(id+"F1.wireOp",EDGE,"E88.0")])],"isStart":true});
            var Q57;
            Q57=makeQuery(id+"F4.opExtrude","CAP_EDGE",EDGE,{"disambiguationData":[OSD([sQuery(id+"F1.wireOp",EDGE,"E86.2")])],"isStart":true});
            var Q58;
            Q58=makeQuery(id+"F4.opExtrude","CAP_EDGE",EDGE,{"disambiguationData":[OSD([sQuery(id+"F1.wireOp",EDGE,"E85.2")])],"isStart":true});
            var Q59;
            Q59=makeQuery(id+"F4.opExtrude","CAP_EDGE",EDGE,{"disambiguationData":[OSD([sQuery(id+"F1.wireOp",EDGE,"E85.3")])],"isStart":true});
            var Q60;
            Q60=makeQuery(id+"F4.opExtrude","CAP_EDGE",EDGE,{"disambiguationData":[OSD([sQuery(id+"F1.wireOp",EDGE,"E86.0")])],"isStart":true});
            var Q61;
            Q61=makeQuery(id+"F4.opExtrude","CAP_EDGE",EDGE,{"disambiguationData":[OSD([sQuery(id+"F1.wireOp",EDGE,"E84.1")])],"isStart":true});
            var Q62;
            Q62=makeQuery(id+"F4.opExtrude","CAP_EDGE",EDGE,{"disambiguationData":[OSD([sQuery(id+"F1.wireOp",EDGE,"E84.2")])],"isStart":true});
            var Q63;
            Q63=makeQuery(id+"F4.opExtrude","CAP_EDGE",EDGE,{"disambiguationData":[OSD([sQuery(id+"F1.wireOp",EDGE,"E84.3")])],"isStart":true});
            var Q64;
            Q64=makeQuery(id+"F4.opExtrude","CAP_EDGE",EDGE,{"disambiguationData":[OSD([sQuery(id+"F1.wireOp",EDGE,"E83.2")])],"isStart":true});
            var Q65;
            Q65=makeQuery(id+"F4.opExtrude","CAP_EDGE",EDGE,{"disambiguationData":[OSD([sQuery(id+"F1.wireOp",EDGE,"E82.3")])],"isStart":true});
            var Q66;
            Q66=makeQuery(id+"F4.opExtrude","CAP_EDGE",EDGE,{"disambiguationData":[OSD([sQuery(id+"F1.wireOp",EDGE,"E83.1")])],"isStart":true});
            var Q67;
            Q67=makeQuery(id+"F4.opExtrude","CAP_EDGE",EDGE,{"disambiguationData":[OSD([sQuery(id+"F1.wireOp",EDGE,"E81.0")])],"isStart":true});
            var Q68;
            Q68=makeQuery(id+"F4.opExtrude","CAP_EDGE",EDGE,{"disambiguationData":[OSD([sQuery(id+"F1.wireOp",EDGE,"E81.1")])],"isStart":true});
            var Q69;
            Q69=makeQuery(id+"F4.opExtrude","CAP_EDGE",EDGE,{"disambiguationData":[OSD([sQuery(id+"F1.wireOp",EDGE,"E81.2")])],"isStart":true});
            var Q70;
            Q70=makeQuery(id+"F4.opExtrude","CAP_EDGE",EDGE,{"disambiguationData":[OSD([sQuery(id+"F1.wireOp",EDGE,"E81.3")])],"isStart":true});
            var Q71;
            Q71=makeQuery(id+"F4.opExtrude","CAP_EDGE",EDGE,{"disambiguationData":[OSD([sQuery(id+"F1.wireOp",EDGE,"E80.0")])],"isStart":true});
            var Q72;
            Q72=makeQuery(id+"F4.opExtrude","CAP_EDGE",EDGE,{"disambiguationData":[OSD([sQuery(id+"F1.wireOp",EDGE,"E80.1")])],"isStart":true});
            var Q73;
            Q73=makeQuery(id+"F4.opExtrude","CAP_EDGE",EDGE,{"disambiguationData":[OSD([sQuery(id+"F1.wireOp",EDGE,"E79.0")])],"isStart":true});
            var Q74;
            Q74=makeQuery(id+"F4.opExtrude","CAP_EDGE",EDGE,{"disambiguationData":[OSD([sQuery(id+"F1.wireOp",EDGE,"E77.4")])],"isStart":true});
            var Q75;
            Q75=makeQuery(id+"F4.opExtrude","CAP_EDGE",EDGE,{"disambiguationData":[OSD([sQuery(id+"F1.wireOp",EDGE,"E77.1")])],"isStart":true});
            var Q76;
            Q76=makeQuery(id+"F4.opExtrude","CAP_EDGE",EDGE,{"disambiguationData":[OSD([sQuery(id+"F1.wireOp",EDGE,"E74.5")])],"isStart":true});
            var Q77;
            Q77=makeQuery(id+"F4.opExtrude","CAP_EDGE",EDGE,{"disambiguationData":[OSD([sQuery(id+"F1.wireOp",EDGE,"E76.0")])],"isStart":true});
            var Q78;
            Q78=makeQuery(id+"F4.opExtrude","CAP_EDGE",EDGE,{"disambiguationData":[OSD([sQuery(id+"F1.wireOp",EDGE,"E73.5")])],"isStart":true});
            var Q79;
            Q79=makeQuery(id+"F4.opExtrude","CAP_EDGE",EDGE,{"disambiguationData":[OSD([sQuery(id+"F1.wireOp",EDGE,"E73.3")])],"isStart":true});
            var Q80;
            Q80=makeQuery(id+"F4.opExtrude","CAP_EDGE",EDGE,{"disambiguationData":[OSD([sQuery(id+"F1.wireOp",EDGE,"E73.0")])],"isStart":true});
            var Q81;
            Q81=makeQuery(id+"F4.opExtrude","CAP_EDGE",EDGE,{"disambiguationData":[OSD([sQuery(id+"F1.wireOp",EDGE,"E88.0")])],"isStart":false});
            var Q82;
            Q82=makeQuery(id+"F4.opExtrude","CAP_EDGE",EDGE,{"disambiguationData":[OSD([sQuery(id+"F1.wireOp",EDGE,"E86.3")])],"isStart":false});
            var Q83;
            Q83=makeQuery(id+"F4.opExtrude","CAP_EDGE",EDGE,{"disambiguationData":[OSD([sQuery(id+"F1.wireOp",EDGE,"E86.2")])],"isStart":false});
            var Q84;
            Q84=makeQuery(id+"F4.opExtrude","CAP_EDGE",EDGE,{"disambiguationData":[OSD([sQuery(id+"F1.wireOp",EDGE,"E86.0")])],"isStart":false});
            var Q85;
            Q85=makeQuery(id+"F4.opExtrude","CAP_EDGE",EDGE,{"disambiguationData":[OSD([sQuery(id+"F1.wireOp",EDGE,"E85.3")])],"isStart":false});
            var Q86;
            Q86=makeQuery(id+"F4.opExtrude","CAP_EDGE",EDGE,{"disambiguationData":[OSD([sQuery(id+"F1.wireOp",EDGE,"E85.1")])],"isStart":false});
            var Q87;
            Q87=makeQuery(id+"F4.opExtrude","SWEPT_EDGE",EDGE,{"disambiguationData":[OSD([sQuery(id+"F1.wireOp",EDGE,"E90.2"),sQuery(id+"F1.wireOp",EDGE,"E90.3")])]});
            var Q88;
            Q88=makeQuery(id+"F4.opExtrude","CAP_EDGE",EDGE,{"disambiguationData":[OSD([sQuery(id+"F1.wireOp",EDGE,"E84.1")])],"isStart":false});
            var Q89;
            Q89=makeQuery(id+"F4.opExtrude","SWEPT_EDGE",EDGE,{"disambiguationData":[OSD([sQuery(id+"F1.wireOp",EDGE,"E93.2"),sQuery(id+"F1.wireOp",EDGE,"E93.3")])]});
            var Q90;
            Q90=makeQuery(id+"F4.opExtrude","CAP_EDGE",EDGE,{"disambiguationData":[OSD([sQuery(id+"F1.wireOp",EDGE,"E83.2")])],"isStart":false});
            var Q91;
            Q91=makeQuery(id+"F4.opExtrude","SWEPT_EDGE",EDGE,{"disambiguationData":[OSD([sQuery(id+"F1.wireOp",EDGE,"E92.0"),sQuery(id+"F1.wireOp",EDGE,"E92.3")])]});
            var Q92;
            Q92=makeQuery(id+"F4.opExtrude","SWEPT_EDGE",EDGE,{"disambiguationData":[OSD([sQuery(id+"F1.wireOp",EDGE,"E90.1"),sQuery(id+"F1.wireOp",EDGE,"E90.2")])]});
            var Q93;
            Q93=makeQuery(id+"F4.opExtrude","SWEPT_EDGE",EDGE,{"disambiguationData":[OSD([sQuery(id+"F1.wireOp",EDGE,"E92.0"),sQuery(id+"F1.wireOp",EDGE,"E92.1")])]});
            var Q94;
            Q94=makeQuery(id+"F4.opExtrude","CAP_EDGE",EDGE,{"disambiguationData":[OSD([sQuery(id+"F1.wireOp",EDGE,"E82.1")])],"isStart":false});
            var Q95;
            Q95=makeQuery(id+"F4.opExtrude","SWEPT_EDGE",EDGE,{"disambiguationData":[OSD([sQuery(id+"F1.wireOp",EDGE,"E92.2"),sQuery(id+"F1.wireOp",EDGE,"E92.3")])]});
            var Q96;
            Q96=makeQuery(id+"F4.opExtrude","CAP_EDGE",EDGE,{"disambiguationData":[OSD([sQuery(id+"F1.wireOp",EDGE,"E82.3")])],"isStart":false});
            var Q97;
            Q97=makeQuery(id+"F4.opExtrude","CAP_EDGE",EDGE,{"disambiguationData":[OSD([sQuery(id+"F1.wireOp",EDGE,"E83.3")])],"isStart":false});
            var Q98;
            Q98=makeQuery(id+"F4.opExtrude","CAP_EDGE",EDGE,{"disambiguationData":[OSD([sQuery(id+"F1.wireOp",EDGE,"E73.1")])],"isStart":true});
            var Q99;
            Q99=makeQuery(id+"F4.opExtrude","CAP_EDGE",EDGE,{"disambiguationData":[OSD([sQuery(id+"F1.wireOp",EDGE,"E88.2")])],"isStart":false});
            var Q100;
            Q100=makeQuery(id+"F4.opExtrude","CAP_EDGE",EDGE,{"disambiguationData":[OSD([sQuery(id+"F1.wireOp",EDGE,"E89.2")])],"isStart":false});
            var Q101;
            Q101=makeQuery(id+"F4.opExtrude","SWEPT_EDGE",EDGE,{"disambiguationData":[OSD([sQuery(id+"F1.wireOp",EDGE,"E93.1"),sQuery(id+"F1.wireOp",EDGE,"E93.2")])]});
            var Q102;
            Q102=makeQuery(id+"F4.opExtrude","SWEPT_EDGE",EDGE,{"disambiguationData":[OSD([sQuery(id+"F1.wireOp",EDGE,"E72.2"),sQuery(id+"F1.wireOp",EDGE,"E72.4")])]});
            var Q103;
            Q103=makeQuery(id+"F4.opExtrude","CAP_EDGE",EDGE,{"disambiguationData":[OSD([sQuery(id+"F1.wireOp",EDGE,"E72.4")])],"isStart":false});
            var Q104;
            Q104=makeQuery(id+"F4.opExtrude","SWEPT_EDGE",EDGE,{"disambiguationData":[OSD([sQuery(id+"F1.wireOp",EDGE,"E73.2"),sQuery(id+"F1.wireOp",EDGE,"E73.4")])]});
            var Q105;
            Q105=makeQuery(id+"F4.opExtrude","SWEPT_EDGE",EDGE,{"disambiguationData":[OSD([sQuery(id+"F1.wireOp",EDGE,"E73.0"),sQuery(id+"F1.wireOp",EDGE,"E73.5")])]});
            var Q106;
            Q106=makeQuery(id+"F4.opExtrude","SWEPT_EDGE",EDGE,{"disambiguationData":[OSD([sQuery(id+"F1.wireOp",EDGE,"E73.1"),sQuery(id+"F1.wireOp",EDGE,"E73.3")])]});
            var Q107;
            Q107=makeQuery(id+"F4.opExtrude","CAP_EDGE",EDGE,{"disambiguationData":[OSD([sQuery(id+"F1.wireOp",EDGE,"E73.1")])],"isStart":false});
            var Q108;
            Q108=makeQuery(id+"F4.opExtrude","CAP_EDGE",EDGE,{"disambiguationData":[OSD([sQuery(id+"F1.wireOp",EDGE,"E73.3")])],"isStart":false});
            var Q109;
            Q109=makeQuery(id+"F4.opExtrude","CAP_EDGE",EDGE,{"disambiguationData":[OSD([sQuery(id+"F1.wireOp",EDGE,"E73.0")])],"isStart":false});
            var Q110;
            Q110=makeQuery(id+"F4.opExtrude","CAP_EDGE",EDGE,{"disambiguationData":[OSD([sQuery(id+"F1.wireOp",EDGE,"E73.5")])],"isStart":false});
            var Q111;
            Q111=makeQuery(id+"F4.opExtrude","CAP_EDGE",EDGE,{"disambiguationData":[OSD([sQuery(id+"F1.wireOp",EDGE,"E76.0")])],"isStart":false});
            var Q112;
            Q112=makeQuery(id+"F4.opExtrude","SWEPT_EDGE",EDGE,{"disambiguationData":[OSD([sQuery(id+"F1.wireOp",EDGE,"E77.2"),sQuery(id+"F1.wireOp",EDGE,"E77.4")])]});
            var Q113;
            Q113=makeQuery(id+"F4.opExtrude","SWEPT_EDGE",EDGE,{"disambiguationData":[OSD([sQuery(id+"F1.wireOp",EDGE,"E77.0"),sQuery(id+"F1.wireOp",EDGE,"E77.3")])]});
            var Q114;
            Q114=makeQuery(id+"F4.opExtrude","SWEPT_EDGE",EDGE,{"disambiguationData":[OSD([sQuery(id+"F1.wireOp",EDGE,"E77.1"),sQuery(id+"F1.wireOp",EDGE,"E77.3")])]});
            var Q115;
            Q115=makeQuery(id+"F4.opExtrude","SWEPT_EDGE",EDGE,{"disambiguationData":[OSD([sQuery(id+"F1.wireOp",EDGE,"E77.1"),sQuery(id+"F1.wireOp",EDGE,"E77.2")])]});
            var Q116;
            Q116=makeQuery(id+"F4.opExtrude","CAP_EDGE",EDGE,{"disambiguationData":[OSD([sQuery(id+"F1.wireOp",EDGE,"E77.1")])],"isStart":false});
            var Q117;
            Q117=makeQuery(id+"F4.opExtrude","CAP_EDGE",EDGE,{"disambiguationData":[OSD([sQuery(id+"F1.wireOp",EDGE,"E77.3")])],"isStart":false});
            var Q118;
            Q118=makeQuery(id+"F4.opExtrude","CAP_EDGE",EDGE,{"disambiguationData":[OSD([sQuery(id+"F1.wireOp",EDGE,"E77.4")])],"isStart":false});
            var Q119;
            Q119=makeQuery(id+"F4.opExtrude","CAP_EDGE",EDGE,{"disambiguationData":[OSD([sQuery(id+"F1.wireOp",EDGE,"E77.2")])],"isStart":false});
            var Q120;
            Q120=makeQuery(id+"F4.opExtrude","CAP_EDGE",EDGE,{"disambiguationData":[OSD([sQuery(id+"F1.wireOp",EDGE,"E77.2")])],"isStart":true});
            var Q121;
            Q121=makeQuery(id+"F4.opExtrude","CAP_EDGE",EDGE,{"disambiguationData":[OSD([sQuery(id+"F1.wireOp",EDGE,"E79.1")])],"isStart":false});
            var Q122;
            Q122=makeQuery(id+"F4.opExtrude","CAP_EDGE",EDGE,{"disambiguationData":[OSD([sQuery(id+"F1.wireOp",EDGE,"E79.2")])],"isStart":false});
            var Q123;
            Q123=makeQuery(id+"F4.opExtrude","CAP_EDGE",EDGE,{"disambiguationData":[OSD([sQuery(id+"F1.wireOp",EDGE,"E79.0")])],"isStart":false});
            var Q124;
            Q124=makeQuery(id+"F4.opExtrude","SWEPT_EDGE",EDGE,{"disambiguationData":[OSD([sQuery(id+"F1.wireOp",EDGE,"E80.0"),sQuery(id+"F1.wireOp",EDGE,"E80.3")])]});
            var Q125;
            Q125=makeQuery(id+"F4.opExtrude","SWEPT_EDGE",EDGE,{"disambiguationData":[OSD([sQuery(id+"F1.wireOp",EDGE,"E80.0"),sQuery(id+"F1.wireOp",EDGE,"E80.1")])]});
            var Q126;
            Q126=makeQuery(id+"F4.opExtrude","CAP_EDGE",EDGE,{"disambiguationData":[OSD([sQuery(id+"F1.wireOp",EDGE,"E80.1")])],"isStart":false});
            var Q127;
            Q127=makeQuery(id+"F4.opExtrude","CAP_EDGE",EDGE,{"disambiguationData":[OSD([sQuery(id+"F1.wireOp",EDGE,"E80.3")])],"isStart":false});
            var Q128;
            Q128=makeQuery(id+"F4.opExtrude","CAP_EDGE",EDGE,{"disambiguationData":[OSD([sQuery(id+"F1.wireOp",EDGE,"E80.0")])],"isStart":false});
            var Q129;
            Q129=makeQuery(id+"F4.opExtrude","CAP_EDGE",EDGE,{"disambiguationData":[OSD([sQuery(id+"F1.wireOp",EDGE,"E80.3")])],"isStart":true});
            var Q130;
            Q130=makeQuery(id+"F4.opExtrude","SWEPT_EDGE",EDGE,{"disambiguationData":[OSD([sQuery(id+"F1.wireOp",EDGE,"E81.1"),sQuery(id+"F1.wireOp",EDGE,"E81.2")])]});
            var Q131;
            Q131=makeQuery(id+"F4.opExtrude","SWEPT_EDGE",EDGE,{"disambiguationData":[OSD([sQuery(id+"F1.wireOp",EDGE,"E81.0"),sQuery(id+"F1.wireOp",EDGE,"E81.1")])]});
            var Q132;
            Q132=makeQuery(id+"F4.opExtrude","CAP_EDGE",EDGE,{"disambiguationData":[OSD([sQuery(id+"F1.wireOp",EDGE,"E81.0")])],"isStart":false});
            var Q133;
            Q133=makeQuery(id+"F4.opExtrude","SWEPT_EDGE",EDGE,{"disambiguationData":[OSD([sQuery(id+"F1.wireOp",EDGE,"E83.2"),sQuery(id+"F1.wireOp",EDGE,"E83.3")])]});
            var Q134;
            Q134=makeQuery(id+"F4.opExtrude","SWEPT_EDGE",EDGE,{"disambiguationData":[OSD([sQuery(id+"F1.wireOp",EDGE,"E83.1"),sQuery(id+"F1.wireOp",EDGE,"E83.2")])]});
            var Q135;
            Q135=makeQuery(id+"F4.opExtrude","CAP_EDGE",EDGE,{"disambiguationData":[OSD([sQuery(id+"F1.wireOp",EDGE,"E83.1")])],"isStart":false});
            var Q136;
            Q136=makeQuery(id+"F4.opExtrude","CAP_EDGE",EDGE,{"disambiguationData":[OSD([sQuery(id+"F1.wireOp",EDGE,"E83.3")])],"isStart":true});
            var Q137;
            Q137=makeQuery(id+"F4.opExtrude","SWEPT_EDGE",EDGE,{"disambiguationData":[OSD([sQuery(id+"F1.wireOp",EDGE,"E84.0"),sQuery(id+"F1.wireOp",EDGE,"E84.3")])]});
            var Q138;
            Q138=makeQuery(id+"F4.opExtrude","SWEPT_EDGE",EDGE,{"disambiguationData":[OSD([sQuery(id+"F1.wireOp",EDGE,"E84.2"),sQuery(id+"F1.wireOp",EDGE,"E84.3")])]});
            var Q139;
            Q139=makeQuery(id+"F4.opExtrude","SWEPT_EDGE",EDGE,{"disambiguationData":[OSD([sQuery(id+"F1.wireOp",EDGE,"E84.0"),sQuery(id+"F1.wireOp",EDGE,"E84.1")])]});
            var Q140;
            Q140=makeQuery(id+"F4.opExtrude","CAP_EDGE",EDGE,{"disambiguationData":[OSD([sQuery(id+"F1.wireOp",EDGE,"E84.3")])],"isStart":false});
            var Q141;
            Q141=makeQuery(id+"F4.opExtrude","SWEPT_EDGE",EDGE,{"disambiguationData":[OSD([sQuery(id+"F1.wireOp",EDGE,"E85.2"),sQuery(id+"F1.wireOp",EDGE,"E85.3")])]});
            var Q142;
            Q142=makeQuery(id+"F4.opExtrude","SWEPT_EDGE",EDGE,{"disambiguationData":[OSD([sQuery(id+"F1.wireOp",EDGE,"E85.1"),sQuery(id+"F1.wireOp",EDGE,"E85.2")])]});
            var Q143;
            Q143=makeQuery(id+"F4.opExtrude","CAP_EDGE",EDGE,{"disambiguationData":[OSD([sQuery(id+"F1.wireOp",EDGE,"E85.2")])],"isStart":false});
            var Q144;
            Q144=makeQuery(id+"F4.opExtrude","CAP_EDGE",EDGE,{"disambiguationData":[OSD([sQuery(id+"F1.wireOp",EDGE,"E85.1")])],"isStart":true});
            var Q145;
            Q145=makeQuery(id+"F4.opExtrude","SWEPT_EDGE",EDGE,{"disambiguationData":[OSD([sQuery(id+"F1.wireOp",EDGE,"E86.0"),sQuery(id+"F1.wireOp",EDGE,"E86.3")])]});
            var Q146;
            Q146=makeQuery(id+"F4.opExtrude","SWEPT_EDGE",EDGE,{"disambiguationData":[OSD([sQuery(id+"F1.wireOp",EDGE,"E86.2"),sQuery(id+"F1.wireOp",EDGE,"E86.3")])]});
            var Q147;
            Q147=makeQuery(id+"F4.opExtrude","SWEPT_EDGE",EDGE,{"disambiguationData":[OSD([sQuery(id+"F1.wireOp",EDGE,"E86.1"),sQuery(id+"F1.wireOp",EDGE,"E86.2")])]});
            var Q148;
            Q148=makeQuery(id+"F4.opExtrude","SWEPT_EDGE",EDGE,{"disambiguationData":[OSD([sQuery(id+"F1.wireOp",EDGE,"E86.0"),sQuery(id+"F1.wireOp",EDGE,"E86.1")])]});
            var Q149;
            Q149=makeQuery(id+"F4.opExtrude","SWEPT_EDGE",EDGE,{"disambiguationData":[OSD([sQuery(id+"F1.wireOp",EDGE,"E88.0"),sQuery(id+"F1.wireOp",EDGE,"E88.3")])]});
            var Q150;
            Q150=makeQuery(id+"F4.opExtrude","SWEPT_EDGE",EDGE,{"disambiguationData":[OSD([sQuery(id+"F1.wireOp",EDGE,"E88.2"),sQuery(id+"F1.wireOp",EDGE,"E88.3")])]});
            var Q151;
            Q151=makeQuery(id+"F4.opExtrude","SWEPT_EDGE",EDGE,{"disambiguationData":[OSD([sQuery(id+"F1.wireOp",EDGE,"E88.1"),sQuery(id+"F1.wireOp",EDGE,"E88.2")])]});
            var Q152;
            Q152=makeQuery(id+"F4.opExtrude","SWEPT_EDGE",EDGE,{"disambiguationData":[OSD([sQuery(id+"F1.wireOp",EDGE,"E88.0"),sQuery(id+"F1.wireOp",EDGE,"E88.1")])]});
            var Q153;
            Q153=makeQuery(id+"F4.opExtrude","SWEPT_EDGE",EDGE,{"disambiguationData":[OSD([sQuery(id+"F1.wireOp",EDGE,"E89.2"),sQuery(id+"F1.wireOp",EDGE,"E89.3")])]});
            var Q154;
            Q154=makeQuery(id+"F4.opExtrude","SWEPT_EDGE",EDGE,{"disambiguationData":[OSD([sQuery(id+"F1.wireOp",EDGE,"E89.1"),sQuery(id+"F1.wireOp",EDGE,"E89.2")])]});
            var Q155;
            Q155=makeQuery(id+"F4.opExtrude","CAP_EDGE",EDGE,{"disambiguationData":[OSD([sQuery(id+"F1.wireOp",EDGE,"E89.2")])],"isStart":true});
            var Q156;
            Q156=makeQuery(id+"F6.opExtrude","CAP_EDGE",EDGE,{"disambiguationData":[OSD([sQuery(id+"F5.wireOp",EDGE,"E99.3")])],"isStart":true});
            var Q157;
            Q157=makeQuery(id+"F6.opExtrude","CAP_EDGE",EDGE,{"disambiguationData":[OSD([sQuery(id+"F5.wireOp",EDGE,"E99.0")])],"isStart":true});
            var Q158;
            Q158=makeQuery(id+"F6.opExtrude","CAP_EDGE",EDGE,{"disambiguationData":[OSD([sQuery(id+"F5.wireOp",EDGE,"E99.1")])],"isStart":true});
            var Q159;
            Q159=makeQuery(id+"F6.opExtrude","CAP_EDGE",EDGE,{"disambiguationData":[OSD([sQuery(id+"F5.wireOp",EDGE,"E99.2")])],"isStart":true});
            var Q160;
            Q160=makeQuery(id+"F6.opExtrude","CAP_EDGE",EDGE,{"disambiguationData":[OSD([sQuery(id+"F5.wireOp",EDGE,"E99.3")])],"isStart":false});
            var Q161;
            Q161=makeQuery(id+"F6.opExtrude","CAP_EDGE",EDGE,{"disambiguationData":[OSD([sQuery(id+"F5.wireOp",EDGE,"E99.1")])],"isStart":false});
            var Q162;
            Q162=makeQuery(id+"F6.opExtrude","CAP_EDGE",EDGE,{"disambiguationData":[OSD([sQuery(id+"F5.wireOp",EDGE,"E98.0")])],"isStart":true});
            var Q163;
            Q163=makeQuery(id+"F6.opExtrude","CAP_EDGE",EDGE,{"disambiguationData":[OSD([sQuery(id+"F5.wireOp",EDGE,"E98.1")])],"isStart":true});
            var Q164;
            Q164=makeQuery(id+"F6.opExtrude","CAP_EDGE",EDGE,{"disambiguationData":[OSD([sQuery(id+"F5.wireOp",EDGE,"E98.2")])],"isStart":true});
            var Q165;
            Q165=makeQuery(id+"F6.opExtrude","CAP_EDGE",EDGE,{"disambiguationData":[OSD([sQuery(id+"F5.wireOp",EDGE,"E98.3")])],"isStart":true});
            var Q166;
            Q166=makeQuery(id+"F6.opExtrude","CAP_EDGE",EDGE,{"disambiguationData":[OSD([sQuery(id+"F5.wireOp",EDGE,"E98.1")])],"isStart":false});
            var Q167;
            Q167=makeQuery(id+"F6.opExtrude","CAP_EDGE",EDGE,{"disambiguationData":[OSD([sQuery(id+"F5.wireOp",EDGE,"E98.3")])],"isStart":false});
            var Q168;
            Q168=makeQuery(id+"F6.opExtrude","CAP_EDGE",EDGE,{"disambiguationData":[OSD([sQuery(id+"F5.wireOp",EDGE,"E97.0")])],"isStart":true});
            var Q169;
            Q169=makeQuery(id+"F6.opExtrude","CAP_EDGE",EDGE,{"disambiguationData":[OSD([sQuery(id+"F5.wireOp",EDGE,"E97.2")])],"isStart":true});
            var Q170;
            Q170=makeQuery(id+"F6.opExtrude","CAP_EDGE",EDGE,{"disambiguationData":[OSD([sQuery(id+"F5.wireOp",EDGE,"E97.0")])],"isStart":false});
            var Q171;
            Q171=makeQuery(id+"F6.opExtrude","CAP_EDGE",EDGE,{"disambiguationData":[OSD([sQuery(id+"F5.wireOp",EDGE,"E97.2")])],"isStart":false});
            var Q172;
            Q172=makeQuery(id+"F6.opExtrude","SWEPT_EDGE",EDGE,{"disambiguationData":[OSD([sQuery(id+"F5.wireOp",EDGE,"E97.0"),sQuery(id+"F5.wireOp",EDGE,"E97.1")])]});
            var Q173;
            Q173=makeQuery(id+"F6.opExtrude","SWEPT_EDGE",EDGE,{"disambiguationData":[OSD([sQuery(id+"F5.wireOp",EDGE,"E97.1"),sQuery(id+"F5.wireOp",EDGE,"E97.2")])]});
            var Q174;
            Q174=makeQuery(id+"F6.opExtrude","SWEPT_EDGE",EDGE,{"disambiguationData":[OSD([sQuery(id+"F5.wireOp",EDGE,"E97.2"),sQuery(id+"F5.wireOp",EDGE,"E97.3")])]});
            var Q175;
            Q175=makeQuery(id+"F6.opExtrude","SWEPT_EDGE",EDGE,{"disambiguationData":[OSD([sQuery(id+"F5.wireOp",EDGE,"E97.0"),sQuery(id+"F5.wireOp",EDGE,"E97.3")])]});
            var Q176;
            Q176=makeQuery(id+"F6.opExtrude","CAP_EDGE",EDGE,{"disambiguationData":[OSD([sQuery(id+"F5.wireOp",EDGE,"E97.3")])],"isStart":false});
            var Q177;
            Q177=makeQuery(id+"F6.opExtrude","CAP_EDGE",EDGE,{"disambiguationData":[OSD([sQuery(id+"F5.wireOp",EDGE,"E96.1")])],"isStart":true});
            var Q178;
            Q178=makeQuery(id+"F6.opExtrude","SWEPT_EDGE",EDGE,{"disambiguationData":[OSD([sQuery(id+"F5.wireOp",EDGE,"E96.2"),sQuery(id+"F5.wireOp",EDGE,"E96.3")])]});
            var Q179;
            Q179=makeQuery(id+"F6.opExtrude","CAP_EDGE",EDGE,{"disambiguationData":[OSD([sQuery(id+"F5.wireOp",EDGE,"E96.0")])],"isStart":true});
            var Q180;
            Q180=makeQuery(id+"F6.opExtrude","SWEPT_EDGE",EDGE,{"disambiguationData":[OSD([sQuery(id+"F5.wireOp",EDGE,"E96.0"),sQuery(id+"F5.wireOp",EDGE,"E96.3")])]});
            var Q181;
            Q181=makeQuery(id+"F6.opExtrude","CAP_EDGE",EDGE,{"disambiguationData":[OSD([sQuery(id+"F5.wireOp",EDGE,"E96.2")])],"isStart":true});
            var Q182;
            Q182=makeQuery(id+"F6.opExtrude","CAP_EDGE",EDGE,{"disambiguationData":[OSD([sQuery(id+"F5.wireOp",EDGE,"E96.2")])],"isStart":false});
            var Q183;
            Q183=makeQuery(id+"F6.opExtrude","CAP_EDGE",EDGE,{"disambiguationData":[OSD([sQuery(id+"F5.wireOp",EDGE,"E96.1")])],"isStart":false});
            var Q184;
            Q184=makeQuery(id+"F6.opExtrude","SWEPT_EDGE",EDGE,{"disambiguationData":[OSD([sQuery(id+"F5.wireOp",EDGE,"E96.0"),sQuery(id+"F5.wireOp",EDGE,"E96.1")])]});
            var Q185;
            Q185=makeQuery(id+"F6.opExtrude","SWEPT_EDGE",EDGE,{"disambiguationData":[OSD([sQuery(id+"F5.wireOp",EDGE,"E96.1"),sQuery(id+"F5.wireOp",EDGE,"E96.2")])]});
            var Q186;
            Q186=makeQuery(id+"F6.opExtrude","CAP_EDGE",EDGE,{"disambiguationData":[OSD([sQuery(id+"F5.wireOp",EDGE,"E96.0")])],"isStart":false});
            var Q187;
            Q187=makeQuery(id+"F6.opExtrude","CAP_EDGE",EDGE,{"disambiguationData":[OSD([sQuery(id+"F5.wireOp",EDGE,"E95.2")])],"isStart":true});
            var Q188;
            Q188=makeQuery(id+"F6.opExtrude","SWEPT_EDGE",EDGE,{"disambiguationData":[OSD([sQuery(id+"F5.wireOp",EDGE,"E95.0"),sQuery(id+"F5.wireOp",EDGE,"E95.3")])]});
            var Q189;
            Q189=makeQuery(id+"F6.opExtrude","CAP_EDGE",EDGE,{"disambiguationData":[OSD([sQuery(id+"F5.wireOp",EDGE,"E95.1")])],"isStart":true});
            var Q190;
            Q190=makeQuery(id+"F6.opExtrude","CAP_EDGE",EDGE,{"disambiguationData":[OSD([sQuery(id+"F5.wireOp",EDGE,"E95.0")])],"isStart":true});
            var Q191;
            Q191=makeQuery(id+"F6.opExtrude","SWEPT_EDGE",EDGE,{"disambiguationData":[OSD([sQuery(id+"F5.wireOp",EDGE,"E95.2"),sQuery(id+"F5.wireOp",EDGE,"E95.3")])]});
            var Q192;
            Q192=makeQuery(id+"F6.opExtrude","CAP_EDGE",EDGE,{"disambiguationData":[OSD([sQuery(id+"F5.wireOp",EDGE,"E95.3")])],"isStart":false});
            var Q193;
            Q193=makeQuery(id+"F6.opExtrude","CAP_EDGE",EDGE,{"disambiguationData":[OSD([sQuery(id+"F5.wireOp",EDGE,"E95.2")])],"isStart":false});
            var Q194;
            Q194=makeQuery(id+"F6.opExtrude","CAP_EDGE",EDGE,{"disambiguationData":[OSD([sQuery(id+"F5.wireOp",EDGE,"E95.1")])],"isStart":false});
            var Q195;
            Q195=makeQuery(id+"F6.opExtrude","CAP_EDGE",EDGE,{"disambiguationData":[OSD([sQuery(id+"F5.wireOp",EDGE,"E95.0")])],"isStart":false});
            var Q196;
            Q196=makeQuery(id+"F4.opExtrude","CAP_EDGE",EDGE,{"disambiguationData":[OSD([sQuery(id+"F1.wireOp",EDGE,"E93.1")])],"isStart":true});
            var Q197;
            Q197=makeQuery(id+"F4.opExtrude","CAP_EDGE",EDGE,{"disambiguationData":[OSD([sQuery(id+"F1.wireOp",EDGE,"E93.1")])],"isStart":false});
            var Q198;
            Q198=makeQuery(id+"F4.opExtrude","CAP_EDGE",EDGE,{"disambiguationData":[OSD([sQuery(id+"F1.wireOp",EDGE,"E92.1")])],"isStart":true});
            var Q199;
            Q199=makeQuery(id+"F4.opExtrude","CAP_EDGE",EDGE,{"disambiguationData":[OSD([sQuery(id+"F1.wireOp",EDGE,"E92.1")])],"isStart":false});
            var Q200;
            Q200=makeQuery(id+"F4.opExtrude","CAP_EDGE",EDGE,{"disambiguationData":[OSD([sQuery(id+"F1.wireOp",EDGE,"E91.0")])],"isStart":true});
            var Q201;
            Q201=makeQuery(id+"F4.opExtrude","CAP_EDGE",EDGE,{"disambiguationData":[OSD([sQuery(id+"F1.wireOp",EDGE,"E91.3")])],"isStart":true});
            var Q202;
            Q202=makeQuery(id+"F4.opExtrude","CAP_EDGE",EDGE,{"disambiguationData":[OSD([sQuery(id+"F1.wireOp",EDGE,"E91.2")])],"isStart":true});
            var Q203;
            Q203=makeQuery(id+"F4.opExtrude","CAP_EDGE",EDGE,{"disambiguationData":[OSD([sQuery(id+"F1.wireOp",EDGE,"E91.0")])],"isStart":false});
            var Q204;
            Q204=makeQuery(id+"F4.opExtrude","CAP_EDGE",EDGE,{"disambiguationData":[OSD([sQuery(id+"F1.wireOp",EDGE,"E91.3")])],"isStart":false});
            var Q205;
            Q205=makeQuery(id+"F4.opExtrude","CAP_EDGE",EDGE,{"disambiguationData":[OSD([sQuery(id+"F1.wireOp",EDGE,"E91.2")])],"isStart":false});
            var Q206;
            Q206=makeQuery(id+"F4.opExtrude","SWEPT_EDGE",EDGE,{"disambiguationData":[OSD([sQuery(id+"F1.wireOp",EDGE,"E91.1"),sQuery(id+"F1.wireOp",EDGE,"E91.2")])]});
            var Q207;
            Q207=makeQuery(id+"F4.opExtrude","CAP_EDGE",EDGE,{"disambiguationData":[OSD([sQuery(id+"F1.wireOp",EDGE,"E90.1")])],"isStart":true});
            var Q208;
            Q208=makeQuery(id+"F4.opExtrude","CAP_EDGE",EDGE,{"disambiguationData":[OSD([sQuery(id+"F1.wireOp",EDGE,"E90.1")])],"isStart":false});
            var Q209;
            Q209=makeQuery(id+"F4.opExtrude","CAP_EDGE",EDGE,{"disambiguationData":[OSD([sQuery(id+"F1.wireOp",EDGE,"E89.0")])],"isStart":true});
            var Q210;
            Q210=makeQuery(id+"F4.opExtrude","CAP_EDGE",EDGE,{"disambiguationData":[OSD([sQuery(id+"F1.wireOp",EDGE,"E89.3")])],"isStart":true});
            var Q211;
            Q211=makeQuery(id+"F4.opExtrude","CAP_EDGE",EDGE,{"disambiguationData":[OSD([sQuery(id+"F1.wireOp",EDGE,"E57.3")])],"isStart":true});
            var Q212;
            Q212=makeQuery(id+"F4.opExtrude","CAP_EDGE",EDGE,{"disambiguationData":[OSD([sQuery(id+"F1.wireOp",EDGE,"E57.1")])],"isStart":true});
            var Q213;
            Q213=makeQuery(id+"F4.opExtrude","SWEPT_EDGE",EDGE,{"disambiguationData":[OSD([sQuery(id+"F1.wireOp",EDGE,"E57.0"),sQuery(id+"F1.wireOp",EDGE,"E57.3")])]});
            var Q214;
            Q214=makeQuery(id+"F3.opExtrude","SWEPT_EDGE",EDGE,{"disambiguationData":[OSD([sQuery(id+"F2.wireOp",EDGE,"E94.top"),sQuery(id+"F2.wireOp",EDGE,"E94.left")])]});
            var Q215;
            Q215=makeQuery(id+"F4.opExtrude","CAP_EDGE",EDGE,{"disambiguationData":[OSD([sQuery(id+"F1.wireOp",EDGE,"E59.0")])],"isStart":true});
            var Q216;
            Q216=makeQuery(id+"F4.opExtrude","CAP_EDGE",EDGE,{"disambiguationData":[OSD([sQuery(id+"F1.wireOp",EDGE,"E65.0")])],"isStart":true});
            var Q217;
            Q217=makeQuery(id+"F4.opExtrude","SWEPT_EDGE",EDGE,{"disambiguationData":[OSD([sQuery(id+"F1.wireOp",EDGE,"E91.2"),sQuery(id+"F1.wireOp",EDGE,"E91.3")])]});
            var Q218;
            Q218=makeQuery(id+"F4.opExtrude","CAP_EDGE",EDGE,{"disambiguationData":[OSD([sQuery(id+"F1.wireOp",EDGE,"E68.0")])],"isStart":true});
            var Q219;
            Q219=makeQuery(id+"F4.opExtrude","CAP_EDGE",EDGE,{"disambiguationData":[OSD([sQuery(id+"F1.wireOp",EDGE,"E71.0")])],"isStart":true});
            var Q220;
            Q220=makeQuery(id+"F4.opExtrude","CAP_EDGE",EDGE,{"disambiguationData":[OSD([sQuery(id+"F1.wireOp",EDGE,"E78.0")])],"isStart":true});
            var Q221;
            Q221=makeQuery(id+"F4.opExtrude","CAP_EDGE",EDGE,{"disambiguationData":[OSD([sQuery(id+"F1.wireOp",EDGE,"E88.3")])],"isStart":true});
            var Q222;
            Q222=makeQuery(id+"F4.opExtrude","CAP_EDGE",EDGE,{"disambiguationData":[OSD([sQuery(id+"F1.wireOp",EDGE,"E89.1")])],"isStart":true});
            var Q223;
            Q223=makeQuery(id+"F4.opExtrude","CAP_EDGE",EDGE,{"disambiguationData":[OSD([sQuery(id+"F1.wireOp",EDGE,"E87.0")])],"isStart":true});
            var Q224;
            Q224=makeQuery(id+"F4.opExtrude","CAP_EDGE",EDGE,{"disambiguationData":[OSD([sQuery(id+"F1.wireOp",EDGE,"E87.2")])],"isStart":true});
            var Q225;
            Q225=makeQuery(id+"F4.opExtrude","CAP_EDGE",EDGE,{"disambiguationData":[OSD([sQuery(id+"F1.wireOp",EDGE,"E86.1")])],"isStart":true});
            var Q226;
            Q226=makeQuery(id+"F4.opExtrude","CAP_EDGE",EDGE,{"disambiguationData":[OSD([sQuery(id+"F1.wireOp",EDGE,"E85.0")])],"isStart":true});
            var Q227;
            Q227=makeQuery(id+"F4.opExtrude","CAP_EDGE",EDGE,{"disambiguationData":[OSD([sQuery(id+"F1.wireOp",EDGE,"E72.3")])],"isStart":false});
            var Q228;
            Q228=makeQuery(id+"F4.opExtrude","CAP_EDGE",EDGE,{"disambiguationData":[OSD([sQuery(id+"F1.wireOp",EDGE,"E82.2")])],"isStart":true});
            var Q229;
            Q229=makeQuery(id+"F4.opExtrude","CAP_EDGE",EDGE,{"disambiguationData":[OSD([sQuery(id+"F1.wireOp",EDGE,"E72.2")])],"isStart":false});
            var Q230;
            Q230=makeQuery(id+"F4.opExtrude","CAP_EDGE",EDGE,{"disambiguationData":[OSD([sQuery(id+"F1.wireOp",EDGE,"E83.0")])],"isStart":true});
            var Q231;
            Q231=makeQuery(id+"F4.opExtrude","CAP_EDGE",EDGE,{"disambiguationData":[OSD([sQuery(id+"F1.wireOp",EDGE,"E72.0")])],"isStart":false});
            var Q232;
            Q232=makeQuery(id+"F4.opExtrude","CAP_EDGE",EDGE,{"disambiguationData":[OSD([sQuery(id+"F1.wireOp",EDGE,"E82.0")])],"isStart":true});
            var Q233;
            Q233=makeQuery(id+"F4.opExtrude","CAP_EDGE",EDGE,{"disambiguationData":[OSD([sQuery(id+"F1.wireOp",EDGE,"E70.0")])],"isStart":false});
            var Q234;
            Q234=makeQuery(id+"F4.opExtrude","CAP_EDGE",EDGE,{"disambiguationData":[OSD([sQuery(id+"F1.wireOp",EDGE,"E71.0")])],"isStart":false});
            var Q235;
            Q235=makeQuery(id+"F4.opExtrude","CAP_EDGE",EDGE,{"disambiguationData":[OSD([sQuery(id+"F1.wireOp",EDGE,"E80.2")])],"isStart":true});
            var Q236;
            Q236=makeQuery(id+"F4.opExtrude","CAP_EDGE",EDGE,{"disambiguationData":[OSD([sQuery(id+"F1.wireOp",EDGE,"E79.2")])],"isStart":true});
            var Q237;
            Q237=makeQuery(id+"F4.opExtrude","CAP_EDGE",EDGE,{"disambiguationData":[OSD([sQuery(id+"F1.wireOp",EDGE,"E79.3")])],"isStart":true});
            var Q238;
            Q238=makeQuery(id+"F4.opExtrude","CAP_EDGE",EDGE,{"disambiguationData":[OSD([sQuery(id+"F1.wireOp",EDGE,"E64.0")])],"isStart":false});
            var Q239;
            Q239=makeQuery(id+"F4.opExtrude","CAP_EDGE",EDGE,{"disambiguationData":[OSD([sQuery(id+"F1.wireOp",EDGE,"E77.3")])],"isStart":true});
            var Q240;
            Q240=makeQuery(id+"F4.opExtrude","CAP_EDGE",EDGE,{"disambiguationData":[OSD([sQuery(id+"F1.wireOp",EDGE,"E77.5")])],"isStart":true});
            var Q241;
            Q241=makeQuery(id+"F4.opExtrude","CAP_EDGE",EDGE,{"disambiguationData":[OSD([sQuery(id+"F1.wireOp",EDGE,"E61.0")])],"isStart":false});
            var Q242;
            Q242=makeQuery(id+"F4.opExtrude","CAP_EDGE",EDGE,{"disambiguationData":[OSD([sQuery(id+"F1.wireOp",EDGE,"E75.0")])],"isStart":true});
            var Q243;
            Q243=makeQuery(id+"F4.opExtrude","CAP_EDGE",EDGE,{"disambiguationData":[OSD([sQuery(id+"F1.wireOp",EDGE,"E77.0")])],"isStart":true});
            var Q244;
            Q244=makeQuery(id+"F4.opExtrude","CAP_EDGE",EDGE,{"disambiguationData":[OSD([sQuery(id+"F1.wireOp",EDGE,"E74.3")])],"isStart":true});
            var Q245;
            Q245=makeQuery(id+"F4.opExtrude","CAP_EDGE",EDGE,{"disambiguationData":[OSD([sQuery(id+"F1.wireOp",EDGE,"E74.0")])],"isStart":true});
            var Q246;
            Q246=makeQuery(id+"F4.opExtrude","CAP_EDGE",EDGE,{"disambiguationData":[OSD([sQuery(id+"F1.wireOp",EDGE,"E74.1")])],"isStart":true});
            var Q247;
            Q247=makeQuery(id+"F4.opExtrude","CAP_EDGE",EDGE,{"disambiguationData":[OSD([sQuery(id+"F1.wireOp",EDGE,"E74.2")])],"isStart":true});
            var Q248;
            Q248=makeQuery(id+"F4.opExtrude","CAP_EDGE",EDGE,{"disambiguationData":[OSD([sQuery(id+"F1.wireOp",EDGE,"E72.5")])],"isStart":true});
            var Q249;
            Q249=makeQuery(id+"F4.opExtrude","CAP_EDGE",EDGE,{"disambiguationData":[OSD([sQuery(id+"F1.wireOp",EDGE,"E85.0")])],"isStart":false});
            var Q250;
            Q250=makeQuery(id+"F4.opExtrude","CAP_EDGE",EDGE,{"disambiguationData":[OSD([sQuery(id+"F1.wireOp",EDGE,"E87.2")])],"isStart":false});
            var Q251;
            Q251=makeQuery(id+"F4.opExtrude","CAP_EDGE",EDGE,{"disambiguationData":[OSD([sQuery(id+"F1.wireOp",EDGE,"E61.0")])],"isStart":true});
            var Q252;
            Q252=makeQuery(id+"F4.opExtrude","CAP_EDGE",EDGE,{"disambiguationData":[OSD([sQuery(id+"F1.wireOp",EDGE,"E66.0")])],"isStart":false});
            var Q253;
            Q253=makeQuery(id+"F4.opExtrude","SWEPT_EDGE",EDGE,{"disambiguationData":[OSD([sQuery(id+"F1.wireOp",EDGE,"E91.0"),sQuery(id+"F1.wireOp",EDGE,"E91.1")])]});
            var Q254;
            Q254=makeQuery(id+"F4.opExtrude","CAP_EDGE",EDGE,{"disambiguationData":[OSD([sQuery(id+"F1.wireOp",EDGE,"E62.0")])],"isStart":true});
            var Q255;
            Q255=makeQuery(id+"F4.opExtrude","CAP_EDGE",EDGE,{"disambiguationData":[OSD([sQuery(id+"F1.wireOp",EDGE,"E87.3")])],"isStart":false});
            var Q256;
            Q256=makeQuery(id+"F4.opExtrude","CAP_EDGE",EDGE,{"disambiguationData":[OSD([sQuery(id+"F1.wireOp",EDGE,"E63.0")])],"isStart":true});
            var Q257;
            Q257=makeQuery(id+"F4.opExtrude","SWEPT_EDGE",EDGE,{"disambiguationData":[OSD([sQuery(id+"F1.wireOp",EDGE,"E91.0"),sQuery(id+"F1.wireOp",EDGE,"E91.3")])]});
            var Q258;
            Q258=makeQuery(id+"F4.opExtrude","SWEPT_EDGE",EDGE,{"disambiguationData":[OSD([sQuery(id+"F1.wireOp",EDGE,"E57.0"),sQuery(id+"F1.wireOp",EDGE,"E57.1")])]});
            var Q259;
            Q259=makeQuery(id+"F4.opExtrude","CAP_EDGE",EDGE,{"disambiguationData":[OSD([sQuery(id+"F1.wireOp",EDGE,"E73.4")])],"isStart":true});
            var Q260;
            Q260=makeQuery(id+"F4.opExtrude","CAP_EDGE",EDGE,{"disambiguationData":[OSD([sQuery(id+"F1.wireOp",EDGE,"E83.0")])],"isStart":false});
            var Q261;
            Q261=makeQuery(id+"F4.opExtrude","CAP_EDGE",EDGE,{"disambiguationData":[OSD([sQuery(id+"F1.wireOp",EDGE,"E58.0")])],"isStart":true});
            var Q262;
            Q262=makeQuery(id+"F4.opExtrude","SWEPT_EDGE",EDGE,{"disambiguationData":[OSD([sQuery(id+"F1.wireOp",EDGE,"E57.1"),sQuery(id+"F1.wireOp",EDGE,"E57.2")])]});
            var Q263;
            Q263=makeQuery(id+"F4.opExtrude","CAP_EDGE",EDGE,{"disambiguationData":[OSD([sQuery(id+"F1.wireOp",EDGE,"E67.0")])],"isStart":true});
            var Q264;
            Q264=makeQuery(id+"F4.opExtrude","CAP_EDGE",EDGE,{"disambiguationData":[OSD([sQuery(id+"F1.wireOp",EDGE,"E64.0")])],"isStart":true});
            var Q265;
            Q265=makeQuery(id+"F4.opExtrude","CAP_EDGE",EDGE,{"disambiguationData":[OSD([sQuery(id+"F1.wireOp",EDGE,"E82.0")])],"isStart":false});
            var Q266;
            Q266=makeQuery(id+"F4.opExtrude","CAP_EDGE",EDGE,{"disambiguationData":[OSD([sQuery(id+"F1.wireOp",EDGE,"E63.0")])],"isStart":false});
            var Q267;
            Q267=makeQuery(id+"F4.opExtrude","SWEPT_EDGE",EDGE,{"disambiguationData":[OSD([sQuery(id+"F1.wireOp",EDGE,"E57.2"),sQuery(id+"F1.wireOp",EDGE,"E57.3")])]});
            var Q268;
            Q268=makeQuery(id+"F4.opExtrude","CAP_EDGE",EDGE,{"disambiguationData":[OSD([sQuery(id+"F1.wireOp",EDGE,"E57.0")])],"isStart":true});
            var Q269;
            Q269=makeQuery(id+"F4.opExtrude","CAP_EDGE",EDGE,{"disambiguationData":[OSD([sQuery(id+"F1.wireOp",EDGE,"E60.0")])],"isStart":true});
            var Q270;
            Q270=makeQuery(id+"F4.opExtrude","CAP_EDGE",EDGE,{"disambiguationData":[OSD([sQuery(id+"F1.wireOp",EDGE,"E66.0")])],"isStart":true});
            var Q271;
            Q271=makeQuery(id+"F4.opExtrude","CAP_EDGE",EDGE,{"disambiguationData":[OSD([sQuery(id+"F1.wireOp",EDGE,"E69.0")])],"isStart":true});
            var Q272;
            Q272=makeQuery(id+"F4.opExtrude","CAP_EDGE",EDGE,{"disambiguationData":[OSD([sQuery(id+"F1.wireOp",EDGE,"E70.0")])],"isStart":true});
            var Q273;
            Q273=makeQuery(id+"F4.opExtrude","CAP_EDGE",EDGE,{"disambiguationData":[OSD([sQuery(id+"F1.wireOp",EDGE,"E72.2")])],"isStart":true});
            var Q274;
            Q274=makeQuery(id+"F4.opExtrude","CAP_EDGE",EDGE,{"disambiguationData":[OSD([sQuery(id+"F1.wireOp",EDGE,"E73.2")])],"isStart":true});
            var Q275;
            Q275=makeQuery(id+"F4.opExtrude","CAP_EDGE",EDGE,{"disambiguationData":[OSD([sQuery(id+"F1.wireOp",EDGE,"E88.3")])],"isStart":false});
            var Q276;
            Q276=makeQuery(id+"F4.opExtrude","CAP_EDGE",EDGE,{"disambiguationData":[OSD([sQuery(id+"F1.wireOp",EDGE,"E89.0")])],"isStart":false});
            var Q277;
            Q277=makeQuery(id+"F4.opExtrude","CAP_EDGE",EDGE,{"disambiguationData":[OSD([sQuery(id+"F1.wireOp",EDGE,"E88.1")])],"isStart":false});
            var Q278;
            Q278=makeQuery(id+"F4.opExtrude","CAP_EDGE",EDGE,{"disambiguationData":[OSD([sQuery(id+"F1.wireOp",EDGE,"E89.3")])],"isStart":false});
            var Q279;
            Q279=makeQuery(id+"F4.opExtrude","CAP_EDGE",EDGE,{"disambiguationData":[OSD([sQuery(id+"F1.wireOp",EDGE,"E89.1")])],"isStart":false});
            var Q280;
            Q280=makeQuery(id+"F4.opExtrude","CAP_EDGE",EDGE,{"disambiguationData":[OSD([sQuery(id+"F1.wireOp",EDGE,"E57.3")])],"isStart":false});
            var Q281;
            Q281=makeQuery(id+"F4.opExtrude","CAP_EDGE",EDGE,{"disambiguationData":[OSD([sQuery(id+"F1.wireOp",EDGE,"E58.0")])],"isStart":false});
            var Q282;
            Q282=makeQuery(id+"F4.opExtrude","CAP_EDGE",EDGE,{"disambiguationData":[OSD([sQuery(id+"F1.wireOp",EDGE,"E57.1")])],"isStart":false});
            var Q283;
            Q283=makeQuery(id+"F4.opExtrude","CAP_EDGE",EDGE,{"disambiguationData":[OSD([sQuery(id+"F1.wireOp",EDGE,"E57.2")])],"isStart":false});
            var Q284;
            Q284=makeQuery(id+"F4.opExtrude","CAP_EDGE",EDGE,{"disambiguationData":[OSD([sQuery(id+"F1.wireOp",EDGE,"E59.0")])],"isStart":false});
            var Q285;
            Q285=makeQuery(id+"F4.opExtrude","CAP_EDGE",EDGE,{"disambiguationData":[OSD([sQuery(id+"F1.wireOp",EDGE,"E60.0")])],"isStart":false});
            var Q286;
            Q286=makeQuery(id+"F4.opExtrude","CAP_EDGE",EDGE,{"disambiguationData":[OSD([sQuery(id+"F1.wireOp",EDGE,"E62.0")])],"isStart":false});
            var Q287;
            Q287=makeQuery(id+"F4.opExtrude","CAP_EDGE",EDGE,{"disambiguationData":[OSD([sQuery(id+"F1.wireOp",EDGE,"E65.0")])],"isStart":false});
            var Q288;
            Q288=makeQuery(id+"F4.opExtrude","CAP_EDGE",EDGE,{"disambiguationData":[OSD([sQuery(id+"F1.wireOp",EDGE,"E72.0")])],"isStart":true});
            var Q289;
            Q289=makeQuery(id+"F4.opExtrude","CAP_EDGE",EDGE,{"disambiguationData":[OSD([sQuery(id+"F1.wireOp",EDGE,"E57.0")])],"isStart":false});
            var Q290;
            Q290=makeQuery(id+"F4.opExtrude","CAP_EDGE",EDGE,{"disambiguationData":[OSD([sQuery(id+"F1.wireOp",EDGE,"E72.3")])],"isStart":true});
            var Q291;
            Q291=makeQuery(id+"F4.opExtrude","CAP_EDGE",EDGE,{"disambiguationData":[OSD([sQuery(id+"F1.wireOp",EDGE,"E67.0")])],"isStart":false});
            var Q292;
            Q292=makeQuery(id+"F4.opExtrude","CAP_EDGE",EDGE,{"disambiguationData":[OSD([sQuery(id+"F1.wireOp",EDGE,"E68.0")])],"isStart":false});
            var Q293;
            Q293=makeQuery(id+"F4.opExtrude","CAP_EDGE",EDGE,{"disambiguationData":[OSD([sQuery(id+"F1.wireOp",EDGE,"E69.0")])],"isStart":false});
            var Q294;
            Q294=makeQuery(id+"F4.opExtrude","SWEPT_EDGE",EDGE,{"disambiguationData":[OSD([sQuery(id+"F1.wireOp",EDGE,"E72.4"),sQuery(id+"F1.wireOp",EDGE,"E72.5")])]});
            var Q295;
            Q295=makeQuery(id+"F4.opExtrude","SWEPT_EDGE",EDGE,{"disambiguationData":[OSD([sQuery(id+"F1.wireOp",EDGE,"E72.0"),sQuery(id+"F1.wireOp",EDGE,"E72.5")])]});
            var Q296;
            Q296=makeQuery(id+"F4.opExtrude","SWEPT_EDGE",EDGE,{"disambiguationData":[OSD([sQuery(id+"F1.wireOp",EDGE,"E72.0"),sQuery(id+"F1.wireOp",EDGE,"E72.3")])]});
            var Q297;
            Q297=makeQuery(id+"F4.opExtrude","CAP_EDGE",EDGE,{"disambiguationData":[OSD([sQuery(id+"F1.wireOp",EDGE,"E72.5")])],"isStart":false});
            var Q298;
            Q298=makeQuery(id+"F4.opExtrude","SWEPT_EDGE",EDGE,{"disambiguationData":[OSD([sQuery(id+"F1.wireOp",EDGE,"E73.4"),sQuery(id+"F1.wireOp",EDGE,"E73.5")])]});
            var Q299;
            Q299=makeQuery(id+"F4.opExtrude","SWEPT_EDGE",EDGE,{"disambiguationData":[OSD([sQuery(id+"F1.wireOp",EDGE,"E73.1"),sQuery(id+"F1.wireOp",EDGE,"E73.2")])]});
            var Q300;
            Q300=makeQuery(id+"F4.opExtrude","CAP_EDGE",EDGE,{"disambiguationData":[OSD([sQuery(id+"F1.wireOp",EDGE,"E73.4")])],"isStart":false});
            var Q301;
            Q301=makeQuery(id+"F4.opExtrude","CAP_EDGE",EDGE,{"disambiguationData":[OSD([sQuery(id+"F1.wireOp",EDGE,"E73.2")])],"isStart":false});
            var Q302;
            Q302=makeQuery(id+"F4.opExtrude","SWEPT_EDGE",EDGE,{"disambiguationData":[OSD([sQuery(id+"F1.wireOp",EDGE,"E74.2"),sQuery(id+"F1.wireOp",EDGE,"E74.4")])]});
            var Q303;
            Q303=makeQuery(id+"F4.opExtrude","SWEPT_EDGE",EDGE,{"disambiguationData":[OSD([sQuery(id+"F1.wireOp",EDGE,"E74.4"),sQuery(id+"F1.wireOp",EDGE,"E74.5")])]});
            var Q304;
            Q304=makeQuery(id+"F4.opExtrude","SWEPT_EDGE",EDGE,{"disambiguationData":[OSD([sQuery(id+"F1.wireOp",EDGE,"E74.0"),sQuery(id+"F1.wireOp",EDGE,"E74.5")])]});
            var Q305;
            Q305=makeQuery(id+"F4.opExtrude","SWEPT_EDGE",EDGE,{"disambiguationData":[OSD([sQuery(id+"F1.wireOp",EDGE,"E74.0"),sQuery(id+"F1.wireOp",EDGE,"E74.3")])]});
            var Q306;
            Q306=makeQuery(id+"F4.opExtrude","SWEPT_EDGE",EDGE,{"disambiguationData":[OSD([sQuery(id+"F1.wireOp",EDGE,"E74.1"),sQuery(id+"F1.wireOp",EDGE,"E74.3")])]});
            var Q307;
            Q307=makeQuery(id+"F4.opExtrude","SWEPT_EDGE",EDGE,{"disambiguationData":[OSD([sQuery(id+"F1.wireOp",EDGE,"E74.1"),sQuery(id+"F1.wireOp",EDGE,"E74.2")])]});
            var Q308;
            Q308=makeQuery(id+"F4.opExtrude","CAP_EDGE",EDGE,{"disambiguationData":[OSD([sQuery(id+"F1.wireOp",EDGE,"E74.1")])],"isStart":false});
            var Q309;
            Q309=makeQuery(id+"F4.opExtrude","CAP_EDGE",EDGE,{"disambiguationData":[OSD([sQuery(id+"F1.wireOp",EDGE,"E74.3")])],"isStart":false});
            var Q310;
            Q310=makeQuery(id+"F4.opExtrude","CAP_EDGE",EDGE,{"disambiguationData":[OSD([sQuery(id+"F1.wireOp",EDGE,"E74.0")])],"isStart":false});
            var Q311;
            Q311=makeQuery(id+"F4.opExtrude","CAP_EDGE",EDGE,{"disambiguationData":[OSD([sQuery(id+"F1.wireOp",EDGE,"E74.5")])],"isStart":false});
            var Q312;
            Q312=makeQuery(id+"F4.opExtrude","CAP_EDGE",EDGE,{"disambiguationData":[OSD([sQuery(id+"F1.wireOp",EDGE,"E74.4")])],"isStart":false});
            var Q313;
            Q313=makeQuery(id+"F4.opExtrude","CAP_EDGE",EDGE,{"disambiguationData":[OSD([sQuery(id+"F1.wireOp",EDGE,"E74.2")])],"isStart":false});
            var Q314;
            Q314=makeQuery(id+"F4.opExtrude","CAP_EDGE",EDGE,{"disambiguationData":[OSD([sQuery(id+"F1.wireOp",EDGE,"E74.4")])],"isStart":true});
            var Q315;
            Q315=makeQuery(id+"F4.opExtrude","CAP_EDGE",EDGE,{"disambiguationData":[OSD([sQuery(id+"F1.wireOp",EDGE,"E75.0")])],"isStart":false});
            var Q316;
            Q316=makeQuery(id+"F4.opExtrude","SWEPT_EDGE",EDGE,{"disambiguationData":[OSD([sQuery(id+"F1.wireOp",EDGE,"E77.4"),sQuery(id+"F1.wireOp",EDGE,"E77.5")])]});
            var Q317;
            Q317=makeQuery(id+"F4.opExtrude","SWEPT_EDGE",EDGE,{"disambiguationData":[OSD([sQuery(id+"F1.wireOp",EDGE,"E77.0"),sQuery(id+"F1.wireOp",EDGE,"E77.5")])]});
            var Q318;
            Q318=makeQuery(id+"F4.opExtrude","CAP_EDGE",EDGE,{"disambiguationData":[OSD([sQuery(id+"F1.wireOp",EDGE,"E77.0")])],"isStart":false});
            var Q319;
            Q319=makeQuery(id+"F4.opExtrude","CAP_EDGE",EDGE,{"disambiguationData":[OSD([sQuery(id+"F1.wireOp",EDGE,"E77.5")])],"isStart":false});
            var Q320;
            Q320=makeQuery(id+"F4.opExtrude","CAP_EDGE",EDGE,{"disambiguationData":[OSD([sQuery(id+"F1.wireOp",EDGE,"E78.0")])],"isStart":false});
            var Q321;
            Q321=makeQuery(id+"F4.opExtrude","SWEPT_EDGE",EDGE,{"disambiguationData":[OSD([sQuery(id+"F1.wireOp",EDGE,"E79.0"),sQuery(id+"F1.wireOp",EDGE,"E79.3")])]});
            var Q322;
            Q322=makeQuery(id+"F4.opExtrude","SWEPT_EDGE",EDGE,{"disambiguationData":[OSD([sQuery(id+"F1.wireOp",EDGE,"E79.0"),sQuery(id+"F1.wireOp",EDGE,"E79.1")])]});
            var Q323;
            Q323=makeQuery(id+"F4.opExtrude","CAP_EDGE",EDGE,{"disambiguationData":[OSD([sQuery(id+"F1.wireOp",EDGE,"E79.3")])],"isStart":false});
            var Q324;
            Q324=makeQuery(id+"F4.opExtrude","CAP_EDGE",EDGE,{"disambiguationData":[OSD([sQuery(id+"F1.wireOp",EDGE,"E79.1")])],"isStart":true});
            var Q325;
            Q325=makeQuery(id+"F4.opExtrude","SWEPT_EDGE",EDGE,{"disambiguationData":[OSD([sQuery(id+"F1.wireOp",EDGE,"E80.2"),sQuery(id+"F1.wireOp",EDGE,"E80.3")])]});
            var Q326;
            Q326=makeQuery(id+"F4.opExtrude","SWEPT_EDGE",EDGE,{"disambiguationData":[OSD([sQuery(id+"F1.wireOp",EDGE,"E80.1"),sQuery(id+"F1.wireOp",EDGE,"E80.2")])]});
            var Q327;
            Q327=makeQuery(id+"F4.opExtrude","CAP_EDGE",EDGE,{"disambiguationData":[OSD([sQuery(id+"F1.wireOp",EDGE,"E80.2")])],"isStart":false});
            var Q328;
            Q328=makeQuery(id+"F4.opExtrude","SWEPT_EDGE",EDGE,{"disambiguationData":[OSD([sQuery(id+"F1.wireOp",EDGE,"E81.0"),sQuery(id+"F1.wireOp",EDGE,"E81.3")])]});
            var Q329;
            Q329=makeQuery(id+"F4.opExtrude","SWEPT_EDGE",EDGE,{"disambiguationData":[OSD([sQuery(id+"F1.wireOp",EDGE,"E81.2"),sQuery(id+"F1.wireOp",EDGE,"E81.3")])]});
            var Q330;
            Q330=makeQuery(id+"F4.opExtrude","SWEPT_EDGE",EDGE,{"disambiguationData":[OSD([sQuery(id+"F1.wireOp",EDGE,"E82.0"),sQuery(id+"F1.wireOp",EDGE,"E82.3")])]});
            var Q331;
            Q331=makeQuery(id+"F4.opExtrude","SWEPT_EDGE",EDGE,{"disambiguationData":[OSD([sQuery(id+"F1.wireOp",EDGE,"E82.2"),sQuery(id+"F1.wireOp",EDGE,"E82.3")])]});
            var Q332;
            Q332=makeQuery(id+"F4.opExtrude","SWEPT_EDGE",EDGE,{"disambiguationData":[OSD([sQuery(id+"F1.wireOp",EDGE,"E82.0"),sQuery(id+"F1.wireOp",EDGE,"E82.1")])]});
            var Q333;
            Q333=makeQuery(id+"F4.opExtrude","CAP_EDGE",EDGE,{"disambiguationData":[OSD([sQuery(id+"F1.wireOp",EDGE,"E82.2")])],"isStart":false});
            var Q334;
            Q334=makeQuery(id+"F4.opExtrude","CAP_EDGE",EDGE,{"disambiguationData":[OSD([sQuery(id+"F1.wireOp",EDGE,"E82.1")])],"isStart":true});
            var Q335;
            Q335=makeQuery(id+"F4.opExtrude","SWEPT_EDGE",EDGE,{"disambiguationData":[OSD([sQuery(id+"F1.wireOp",EDGE,"E83.0"),sQuery(id+"F1.wireOp",EDGE,"E83.3")])]});
            var Q336;
            Q336=makeQuery(id+"F4.opExtrude","SWEPT_EDGE",EDGE,{"disambiguationData":[OSD([sQuery(id+"F1.wireOp",EDGE,"E83.0"),sQuery(id+"F1.wireOp",EDGE,"E83.1")])]});
            var Q337;
            Q337=makeQuery(id+"F4.opExtrude","SWEPT_EDGE",EDGE,{"disambiguationData":[OSD([sQuery(id+"F1.wireOp",EDGE,"E84.1"),sQuery(id+"F1.wireOp",EDGE,"E84.2")])]});
            var Q338;
            Q338=makeQuery(id+"F4.opExtrude","SWEPT_EDGE",EDGE,{"disambiguationData":[OSD([sQuery(id+"F1.wireOp",EDGE,"E85.0"),sQuery(id+"F1.wireOp",EDGE,"E85.3")])]});
            var Q339;
            Q339=makeQuery(id+"F4.opExtrude","SWEPT_EDGE",EDGE,{"disambiguationData":[OSD([sQuery(id+"F1.wireOp",EDGE,"E85.0"),sQuery(id+"F1.wireOp",EDGE,"E85.1")])]});
            var Q340;
            Q340=makeQuery(id+"F4.opExtrude","CAP_EDGE",EDGE,{"disambiguationData":[OSD([sQuery(id+"F1.wireOp",EDGE,"E86.1")])],"isStart":false});
            var Q341;
            Q341=makeQuery(id+"F4.opExtrude","CAP_EDGE",EDGE,{"disambiguationData":[OSD([sQuery(id+"F1.wireOp",EDGE,"E86.3")])],"isStart":true});
            var Q342;
            Q342=makeQuery(id+"F4.opExtrude","SWEPT_EDGE",EDGE,{"disambiguationData":[OSD([sQuery(id+"F1.wireOp",EDGE,"E87.0"),sQuery(id+"F1.wireOp",EDGE,"E87.3")])]});
            var Q343;
            Q343=makeQuery(id+"F4.opExtrude","SWEPT_EDGE",EDGE,{"disambiguationData":[OSD([sQuery(id+"F1.wireOp",EDGE,"E87.2"),sQuery(id+"F1.wireOp",EDGE,"E87.3")])]});
            var Q344;
            Q344=makeQuery(id+"F4.opExtrude","SWEPT_EDGE",EDGE,{"disambiguationData":[OSD([sQuery(id+"F1.wireOp",EDGE,"E87.1"),sQuery(id+"F1.wireOp",EDGE,"E87.2")])]});
            var Q345;
            Q345=makeQuery(id+"F4.opExtrude","SWEPT_EDGE",EDGE,{"disambiguationData":[OSD([sQuery(id+"F1.wireOp",EDGE,"E87.0"),sQuery(id+"F1.wireOp",EDGE,"E87.1")])]});
            var Q346;
            Q346=makeQuery(id+"F4.opExtrude","CAP_EDGE",EDGE,{"disambiguationData":[OSD([sQuery(id+"F1.wireOp",EDGE,"E87.0")])],"isStart":false});
            var Q347;
            Q347=makeQuery(id+"F4.opExtrude","CAP_EDGE",EDGE,{"disambiguationData":[OSD([sQuery(id+"F1.wireOp",EDGE,"E88.1")])],"isStart":true});
            var Q348;
            Q348=makeQuery(id+"F4.opExtrude","SWEPT_EDGE",EDGE,{"disambiguationData":[OSD([sQuery(id+"F1.wireOp",EDGE,"E89.0"),sQuery(id+"F1.wireOp",EDGE,"E89.3")])]});
            var Q349;
            Q349=makeQuery(id+"F4.opExtrude","SWEPT_EDGE",EDGE,{"disambiguationData":[OSD([sQuery(id+"F1.wireOp",EDGE,"E89.0"),sQuery(id+"F1.wireOp",EDGE,"E89.1")])]});
            var Q350;
            Q350=makeQuery(id+"F6.opExtrude","CAP_EDGE",EDGE,{"disambiguationData":[OSD([sQuery(id+"F5.wireOp",EDGE,"E97.1")])],"isStart":true});
            var Q351;
            Q351=makeQuery(id+"F6.opExtrude","CAP_EDGE",EDGE,{"disambiguationData":[OSD([sQuery(id+"F5.wireOp",EDGE,"E97.1")])],"isStart":false});
            var Q352;
            Q352=makeQuery(id+"F6.opExtrude","CAP_EDGE",EDGE,{"disambiguationData":[OSD([sQuery(id+"F5.wireOp",EDGE,"E97.3")])],"isStart":true});
            var Q353;
            Q353=makeQuery(id+"F6.opExtrude","CAP_EDGE",EDGE,{"disambiguationData":[OSD([sQuery(id+"F5.wireOp",EDGE,"E96.3")])],"isStart":true});
            var Q354;
            Q354=makeQuery(id+"F6.opExtrude","CAP_EDGE",EDGE,{"disambiguationData":[OSD([sQuery(id+"F5.wireOp",EDGE,"E96.3")])],"isStart":false});
            var Q355;
            Q355=makeQuery(id+"F6.opExtrude","CAP_EDGE",EDGE,{"disambiguationData":[OSD([sQuery(id+"F5.wireOp",EDGE,"E95.3")])],"isStart":true});
            var Q356;
            Q356=makeQuery(id+"F4.opExtrude","CAP_EDGE",EDGE,{"disambiguationData":[OSD([sQuery(id+"F1.wireOp",EDGE,"E91.1")])],"isStart":true});
            var Q357;
            Q357=makeQuery(id+"F4.opExtrude","CAP_EDGE",EDGE,{"disambiguationData":[OSD([sQuery(id+"F1.wireOp",EDGE,"E91.1")])],"isStart":false});
            var Q358;
            Q358=makeQuery(id+"F3.opExtrude","SWEPT_EDGE",EDGE,{"disambiguationData":[OSD([sQuery(id+"F2.wireOp",EDGE,"E94.top"),sQuery(id+"F2.wireOp",EDGE,"E94.right")])]});
            var Q359;
            Q359=makeQuery(id+"F4.opExtrude","CAP_EDGE",EDGE,{"disambiguationData":[OSD([sQuery(id+"F1.wireOp",EDGE,"E87.1")])],"isStart":true});
            var Q360;
            Q360=makeQuery(id+"F4.opExtrude","CAP_EDGE",EDGE,{"disambiguationData":[OSD([sQuery(id+"F1.wireOp",EDGE,"E87.3")])],"isStart":true});
            var Q361;
            Q361=makeQuery(id+"F4.opExtrude","CAP_EDGE",EDGE,{"disambiguationData":[OSD([sQuery(id+"F1.wireOp",EDGE,"E72.1")])],"isStart":false});
            var Q362;
            Q362=makeQuery(id+"F4.opExtrude","CAP_EDGE",EDGE,{"disambiguationData":[OSD([sQuery(id+"F1.wireOp",EDGE,"E87.1")])],"isStart":false});
            var Q363;
            Q363=makeQuery(id+"F4.opExtrude","CAP_EDGE",EDGE,{"disambiguationData":[OSD([sQuery(id+"F1.wireOp",EDGE,"E72.1")])],"isStart":true});
            var Q364;
            Q364=makeQuery(id+"F4.opExtrude","SWEPT_EDGE",EDGE,{"disambiguationData":[OSD([sQuery(id+"F1.wireOp",EDGE,"E72.1"),sQuery(id+"F1.wireOp",EDGE,"E72.3")])]});
            var Q365;
            Q365=makeQuery(id+"F4.opExtrude","SWEPT_EDGE",EDGE,{"disambiguationData":[OSD([sQuery(id+"F1.wireOp",EDGE,"E72.1"),sQuery(id+"F1.wireOp",EDGE,"E72.2")])]});
            var Q366;
            Q366=makeQuery(id+"F4.opExtrude","CAP_EDGE",EDGE,{"disambiguationData":[OSD([sQuery(id+"F1.wireOp",EDGE,"E72.4")])],"isStart":true});
            var Q367;
            Q367=makeQuery(id+"F4.opExtrude","SWEPT_EDGE",EDGE,{"disambiguationData":[OSD([sQuery(id+"F1.wireOp",EDGE,"E79.2"),sQuery(id+"F1.wireOp",EDGE,"E79.3")])]});
            var Q368;
            Q368=makeQuery(id+"F4.opExtrude","SWEPT_EDGE",EDGE,{"disambiguationData":[OSD([sQuery(id+"F1.wireOp",EDGE,"E79.1"),sQuery(id+"F1.wireOp",EDGE,"E79.2")])]});
            var Q369;
            Q369=makeQuery(id+"F4.opExtrude","SWEPT_EDGE",EDGE,{"disambiguationData":[OSD([sQuery(id+"F1.wireOp",EDGE,"E82.1"),sQuery(id+"F1.wireOp",EDGE,"E82.2")])]});
            fillet(context, id + "F7", {"entities" : qUnion([Q0, Q1, Q2, Q3, Q4, Q5, Q6, Q7, Q8, Q9, Q10, Q11, Q12, Q13, Q14, Q15, Q16, Q17, Q18, Q19, Q20, Q21, Q22, Q23, Q24, Q25, Q26, Q27, Q28, Q29, Q30, Q31, Q32, Q33, Q34, Q35, Q36, Q37, Q38, Q39, Q40, Q41, Q42, Q43, Q44, Q45, Q46, Q47, Q48, Q49, Q50, Q51, Q52, Q53, Q54, Q55, Q56, Q57, Q58, Q59, Q60, Q61, Q62, Q63, Q64, Q65, Q66, Q67, Q68, Q69, Q70, Q71, Q72, Q73, Q74, Q75, Q76, Q77, Q78, Q79, Q80, Q81, Q82, Q83, Q84, Q85, Q86, Q87, Q88, Q89, Q90, Q91, Q92, Q93, Q94, Q95, Q96, Q97, Q98, Q99, Q100, Q101, Q102, Q103, Q104, Q105, Q106, Q107, Q108, Q109, Q110, Q111, Q112, Q113, Q114, Q115, Q116, Q117, Q118, Q119, Q120, Q121, Q122, Q123, Q124, Q125, Q126, Q127, Q128, Q129, Q130, Q131, Q132, Q133, Q134, Q135, Q136, Q137, Q138, Q139, Q140, Q141, Q142, Q143, Q144, Q145, Q146, Q147, Q148, Q149, Q150, Q151, Q152, Q153, Q154, Q155, Q156, Q157, Q158, Q159, Q160, Q161, Q162, Q163, Q164, Q165, Q166, Q167, Q168, Q169, Q170, Q171, Q172, Q173, Q174, Q175, Q176, Q177, Q178, Q179, Q180, Q181, Q182, Q183, Q184, Q185, Q186, Q187, Q188, Q189, Q190, Q191, Q192, Q193, Q194, Q195, Q196, Q197, Q198, Q199, Q200, Q201, Q202, Q203, Q204, Q205, Q206, Q207, Q208, Q209, Q210, Q211, Q212, Q213, Q214, Q215, Q216, Q217, Q218, Q219, Q220, Q221, Q222, Q223, Q224, Q225, Q226, Q227, Q228, Q229, Q230, Q231, Q232, Q233, Q234, Q235, Q236, Q237, Q238, Q239, Q240, Q241, Q242, Q243, Q244, Q245, Q246, Q247, Q248, Q249, Q250, Q251, Q252, Q253, Q254, Q255, Q256, Q257, Q258, Q259, Q260, Q261, Q262, Q263, Q264, Q265, Q266, Q267, Q268, Q269, Q270, Q271, Q272, Q273, Q274, Q275, Q276, Q277, Q278, Q279, Q280, Q281, Q282, Q283, Q284, Q285, Q286, Q287, Q288, Q289, Q290, Q291, Q292, Q293, Q294, Q295, Q296, Q297, Q298, Q299, Q300, Q301, Q302, Q303, Q304, Q305, Q306, Q307, Q308, Q309, Q310, Q311, Q312, Q313, Q314, Q315, Q316, Q317, Q318, Q319, Q320, Q321, Q322, Q323, Q324, Q325, Q326, Q327, Q328, Q329, Q330, Q331, Q332, Q333, Q334, Q335, Q336, Q337, Q338, Q339, Q340, Q341, Q342, Q343, Q344, Q345, Q346, Q347, Q348, Q349, Q350, Q351, Q352, Q353, Q354, Q355, Q356, Q357, Q358, Q359, Q360, Q361, Q362, Q363, Q364, Q365, Q366, Q367, Q368, Q369]), "radius" : 0.13 * mm, "tangentPropagation" : true, "allowEdgeOverflow" : false});
        }
    });
